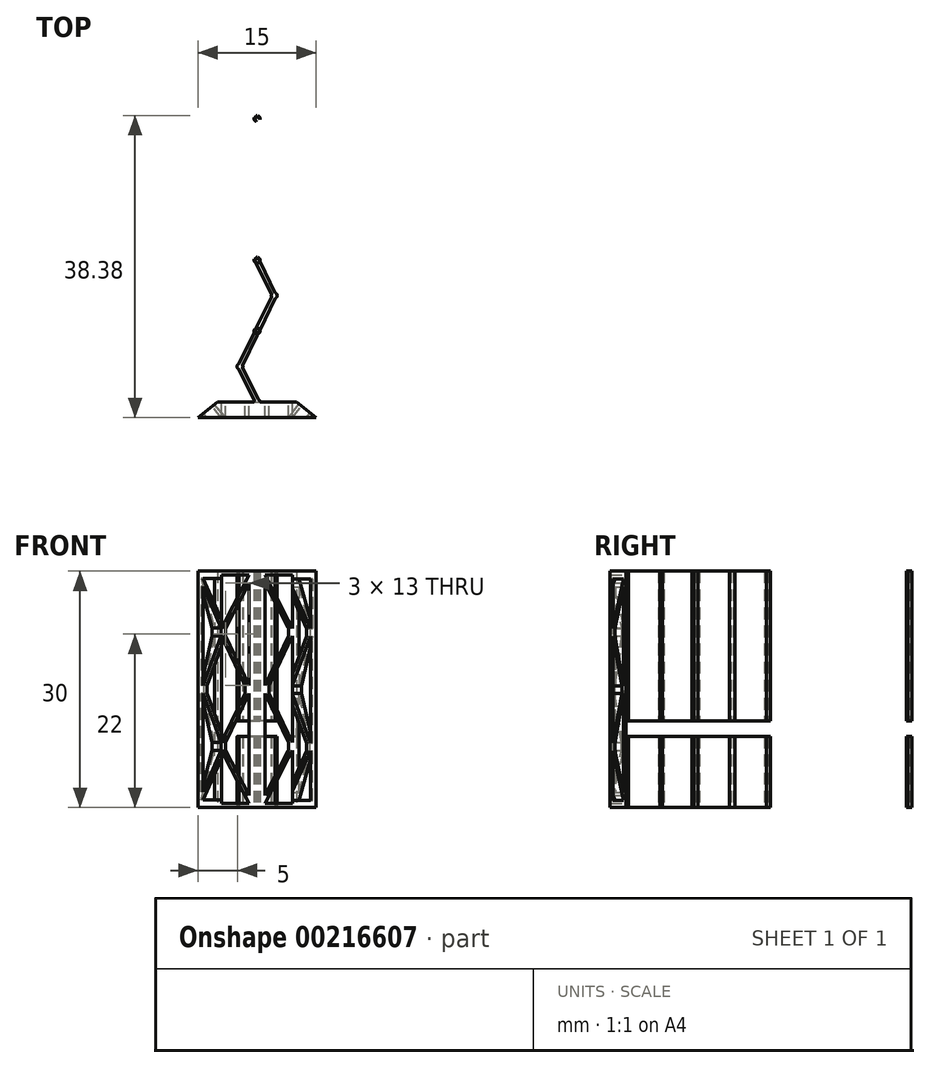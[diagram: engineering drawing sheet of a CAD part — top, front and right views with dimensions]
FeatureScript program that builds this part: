
annotation { "Feature Type Name" : "Feature", "Feature Type Description" : "" }
export const myFeature = defineFeature(function(context is Context, id is Id, definition is map)
    precondition{}
    {
        {
            var Q0;
            Q0=qCreatedBy(makeId("Top.planeOp"),FACE);
            var sketch = newSketch(context, id + "F0", { "sketchPlane" : qUnion([Q0])});
            skLineSegment(sketch, "E0", {"start": v(0, 0) * mm, "end": v(-7.5, 0) * mm});
            skLineSegment(sketch, "E1", {"start": v(0, 0) * mm, "end": v(7.5, 0) * mm});
            skLineSegment(sketch, "E2", {"start": v(0, 0) * mm, "end": v(0, 2) * mm});
            skLineSegment(sketch, "E3", {"start": v(0, 2) * mm, "end": v(-5, 2) * mm});
            skLineSegment(sketch, "E4", {"start": v(-5, 2) * mm, "end": v(-7.5, 0) * mm});
            skLineSegment(sketch, "E5", {"start": v(0, 2) * mm, "end": v(5, 2) * mm});
            skLineSegment(sketch, "E6", {"start": v(5, 2) * mm, "end": v(7.5, 0) * mm});
            skSolve(sketch);
        }
        {
            var Q0;
            Q0=makeQuery(id+"F0.imprint","IMPRINT",FACE,{"disambiguationData":[TD([[makeQuery(id+"F0.imprint","IMPRINT",EDGE,{"derivedFrom":sQuery(id+"F0.wireOp",EDGE,"E0")}),-1.0]])]});
            var Q1;
            Q1=makeQuery(id+"F0.imprint","IMPRINT",FACE,{"disambiguationData":[TD([[makeQuery(id+"F0.imprint","IMPRINT",EDGE,{"derivedFrom":sQuery(id+"F0.wireOp",EDGE,"E1")}),1.0]])]});
            extrude(context, id + "F1", {"entities" : qUnion([Q0, Q1]), "depth" : 30 * mm});
        }
        {
            var Q0;
            Q0=makeQuery(id+"F1.opExtrude","SWEPT_FACE",FACE,{"disambiguationData":[OSD([sQuery(id+"F0.wireOp",EDGE,"E3"),sQuery(id+"F0.wireOp",EDGE,"E5")])]});
            var sketch = newSketch(context, id + "F2", { "sketchPlane" : qUnion([Q0])});
            skLineSegment(sketch, "E7", {"start": v(-5, 30) * mm, "end": v(-5, 29.5) * mm});
            skLineSegment(sketch, "E8", {"start": v(-5, 30) * mm, "end": v(0, 30) * mm});
            skLineSegment(sketch, "E9", {"start": v(0, 30) * mm, "end": v(-1, 30) * mm});
            skLineSegment(sketch, "E10", {"start": v(-5, 29.5) * mm, "end": v(-4.5, 29.5) * mm});
            skLineSegment(sketch, "E11", {"start": v(-1, 30) * mm, "end": v(-5, 30) * mm});
            skLineSegment(sketch, "E12", {"start": v(-5, 29.5) * mm, "end": v(-5, 0) * mm});
            skLineSegment(sketch, "E13", {"start": v(-1, 30) * mm, "end": v(-1, 0) * mm});
            skLineSegment(sketch, "E14", {"start": v(0, 0) * mm, "end": v(-1, 0) * mm});
            skLineSegment(sketch, "E15", {"start": v(-1, 0) * mm, "end": v(-5, 0) * mm});
            skLineSegment(sketch, "E16", {"start": v(-5, 0) * mm, "end": v(-5, 0.5) * mm});
            skLineSegment(sketch, "E17", {"start": v(-5, 0.5) * mm, "end": v(-5, 29.5) * mm});
            skLineSegment(sketch, "E18", {"start": v(-5, 0.5) * mm, "end": v(-4.5, 0.5) * mm});
            skLineSegment(sketch, "E19", {"start": v(-4.5, 29.5) * mm, "end": v(-1, 29.5) * mm});
            skLineSegment(sketch, "E20", {"start": v(-4.5, 0.5) * mm, "end": v(-4.5, 0) * mm});
            skLineSegment(sketch, "E21", {"start": v(-4.5, 0.5) * mm, "end": v(-1, 0.5) * mm});
            skLineSegment(sketch, "E22", {"start": v(-4.5, 15) * mm, "end": v(-1, 15) * mm});
            skLineSegment(sketch, "E23", {"start": v(-4.5, 29.5) * mm, "end": v(-4.5, 15) * mm});
            skLineSegment(sketch, "E24", {"start": v(-4.5, 22.25) * mm, "end": v(-4.5, 22.75) * mm});
            skLineSegment(sketch, "E25", {"start": v(-4.5, 22.25) * mm, "end": v(-4.5, 21.75) * mm});
            skLineSegment(sketch, "E26", {"start": v(-1, 29.5) * mm, "end": v(-4.5, 22.75) * mm});
            skLineSegment(sketch, "E27", {"start": v(-1, 15) * mm, "end": v(-1, 15.5) * mm});
            skLineSegment(sketch, "E28", {"start": v(-1, 29.5) * mm, "end": v(-1, 28.5) * mm});
            skLineSegment(sketch, "E29", {"start": v(-4.5, 22.75) * mm, "end": v(-4, 22.75) * mm});
            skLineSegment(sketch, "E30", {"start": v(-4, 22.75) * mm, "end": v(-1, 28.5) * mm});
            skLineSegment(sketch, "E31", {"start": v(-4, 22.75) * mm, "end": v(-4, 21.75) * mm});
            skLineSegment(sketch, "E32", {"start": v(-4, 21.75) * mm, "end": v(-1, 15.5) * mm});
            skLineSegment(sketch, "E33", {"start": v(-1, 15.5) * mm, "end": v(-1.5, 15.5) * mm});
            skLineSegment(sketch, "E34", {"start": v(-1.5, 15.5) * mm, "end": v(-4.5, 21.75) * mm});
            skLineSegment(sketch, "E35", {"start": v(-1.5, 15.5) * mm, "end": v(-1.5, 15) * mm});
            skLineSegment(sketch, "E36.MirrorCS", {"start": v(-1, 15) * mm, "end": v(-1, 14.5) * mm});
            skLineSegment(sketch, "E37.MirrorCS", {"start": v(-1, 14.5) * mm, "end": v(-1.5, 14.5) * mm});
            skLineSegment(sketch, "E38.MirrorCS", {"start": v(-1.5, 14.5) * mm, "end": v(-1.5, 15) * mm});
            skLineSegment(sketch, "E39.MirrorCS", {"start": v(-4.5, 7.75) * mm, "end": v(-4.5, 8.25) * mm});
            skLineSegment(sketch, "E40.MirrorCS", {"start": v(-4, 7.25) * mm, "end": v(-4, 8.25) * mm});
            skLineSegment(sketch, "E41.MirrorCS", {"start": v(-1, 0.5) * mm, "end": v(-1, 1.5) * mm});
            skLineSegment(sketch, "E42.MirrorCS", {"start": v(-5, 0) * mm, "end": v(0, 0) * mm});
            skLineSegment(sketch, "E43.MirrorCS", {"start": v(-1.5, 14.5) * mm, "end": v(-4.5, 8.25) * mm});
            skLineSegment(sketch, "E44.MirrorCS", {"start": v(-4.5, 0.5) * mm, "end": v(-4.5, 15) * mm});
            skLineSegment(sketch, "E45.MirrorCS", {"start": v(-4, 8.25) * mm, "end": v(-1, 14.5) * mm});
            skLineSegment(sketch, "E46.MirrorCS", {"start": v(-1, 0.5) * mm, "end": v(-4.5, 7.25) * mm});
            skLineSegment(sketch, "E47.MirrorCS", {"start": v(-4, 7.25) * mm, "end": v(-1, 1.5) * mm});
            skLineSegment(sketch, "E48.MirrorCS", {"start": v(-4.5, 7.75) * mm, "end": v(-4.5, 7.25) * mm});
            skLineSegment(sketch, "E49.MirrorCS", {"start": v(-4.5, 7.25) * mm, "end": v(-4, 7.25) * mm});
            skLineSegment(sketch, "E50.MirrorCS", {"start": v(5, 0) * mm, "end": v(5, 0.5) * mm});
            skLineSegment(sketch, "E51.MirrorCS", {"start": v(5, 0.5) * mm, "end": v(4.5, 0.5) * mm});
            skLineSegment(sketch, "E52.MirrorCS", {"start": v(4.5, 0.5) * mm, "end": v(4.5, 0) * mm});
            skLineSegment(sketch, "E53.MirrorCS", {"start": v(4.5, 22.75) * mm, "end": v(4, 22.75) * mm});
            skLineSegment(sketch, "E54.MirrorCS", {"start": v(5, 29.5) * mm, "end": v(4.5, 29.5) * mm});
            skLineSegment(sketch, "E55.MirrorCS", {"start": v(5, 30) * mm, "end": v(5, 29.5) * mm});
            skLineSegment(sketch, "E56.MirrorCS", {"start": v(1, 15.5) * mm, "end": v(1.5, 15.5) * mm});
            skLineSegment(sketch, "E57.MirrorCS", {"start": v(4.5, 7.25) * mm, "end": v(4, 7.25) * mm});
            skLineSegment(sketch, "E58.MirrorCS", {"start": v(1.5, 14.5) * mm, "end": v(1.5, 15) * mm});
            skLineSegment(sketch, "E59.MirrorCS", {"start": v(1, 14.5) * mm, "end": v(1.5, 14.5) * mm});
            skLineSegment(sketch, "E60.MirrorCS", {"start": v(1.5, 15.5) * mm, "end": v(1.5, 15) * mm});
            skLineSegment(sketch, "E61.MirrorCS", {"start": v(4.5, 22.25) * mm, "end": v(4.5, 22.75) * mm});
            skLineSegment(sketch, "E62.MirrorCS", {"start": v(1, 15) * mm, "end": v(1, 14.5) * mm});
            skLineSegment(sketch, "E63.MirrorCS", {"start": v(1, 15) * mm, "end": v(1, 15.5) * mm});
            skLineSegment(sketch, "E64.MirrorCS", {"start": v(4.5, 7.75) * mm, "end": v(4.5, 7.25) * mm});
            skLineSegment(sketch, "E65.MirrorCS", {"start": v(4, 7.25) * mm, "end": v(4, 8.25) * mm});
            skLineSegment(sketch, "E66.MirrorCS", {"start": v(4.5, 7.75) * mm, "end": v(4.5, 8.25) * mm});
            skLineSegment(sketch, "E67.MirrorCS", {"start": v(4.5, 22.25) * mm, "end": v(4.5, 21.75) * mm});
            skLineSegment(sketch, "E68.MirrorCS", {"start": v(1, 0.5) * mm, "end": v(1, 1.5) * mm});
            skLineSegment(sketch, "E69.MirrorCS", {"start": v(1, 29.5) * mm, "end": v(1, 28.5) * mm});
            skLineSegment(sketch, "E70.MirrorCS", {"start": v(4, 22.75) * mm, "end": v(4, 21.75) * mm});
            skLineSegment(sketch, "E71.MirrorCS", {"start": v(1, 0) * mm, "end": v(5, 0) * mm});
            skLineSegment(sketch, "E72.MirrorCS", {"start": v(4.5, 0.5) * mm, "end": v(1, 0.5) * mm});
            skLineSegment(sketch, "E73.MirrorCS", {"start": v(5, 29.5) * mm, "end": v(5, 0) * mm});
            skLineSegment(sketch, "E74.MirrorCS", {"start": v(1, 29.5) * mm, "end": v(4.5, 22.75) * mm});
            skLineSegment(sketch, "E75.MirrorCS", {"start": v(1, 0.5) * mm, "end": v(4.5, 7.25) * mm});
            skLineSegment(sketch, "E76.MirrorCS", {"start": v(1.5, 14.5) * mm, "end": v(4.5, 8.25) * mm});
            skLineSegment(sketch, "E77.MirrorCS", {"start": v(4.5, 29.5) * mm, "end": v(1, 29.5) * mm});
            skLineSegment(sketch, "E78.MirrorCS", {"start": v(4, 21.75) * mm, "end": v(1, 15.5) * mm});
            skLineSegment(sketch, "E79.MirrorCS", {"start": v(5, 0.5) * mm, "end": v(5, 29.5) * mm});
            skLineSegment(sketch, "E80.MirrorCS", {"start": v(4, 8.25) * mm, "end": v(1, 14.5) * mm});
            skLineSegment(sketch, "E81.MirrorCS", {"start": v(4, 7.25) * mm, "end": v(1, 1.5) * mm});
            skLineSegment(sketch, "E82.MirrorCS", {"start": v(1.5, 15.5) * mm, "end": v(4.5, 21.75) * mm});
            skLineSegment(sketch, "E83.MirrorCS", {"start": v(4.5, 0.5) * mm, "end": v(4.5, 15) * mm});
            skLineSegment(sketch, "E84.MirrorCS", {"start": v(1, 30) * mm, "end": v(5, 30) * mm});
            skLineSegment(sketch, "E85.MirrorCS", {"start": v(4.5, 15) * mm, "end": v(1, 15) * mm});
            skLineSegment(sketch, "E86.MirrorCS", {"start": v(1, 30) * mm, "end": v(1, 0) * mm});
            skLineSegment(sketch, "E87.MirrorCS", {"start": v(4, 22.75) * mm, "end": v(1, 28.5) * mm});
            skLineSegment(sketch, "E88.MirrorCS", {"start": v(4.5, 29.5) * mm, "end": v(4.5, 15) * mm});
            skSolve(sketch);
        }
        {
            var Q0;
            {var subQ0=sQuery(id+"F2.wireOp",EDGE,"E19");Q0=makeQuery(id+"F2.imprint","IMPRINT",FACE,{"disambiguationData":[TD([[makeQuery(id+"F2.imprint","IMPRINT",EDGE,{"derivedFrom":subQ0}),-1.0]])]});}
            var Q1;
            {var subQ2=sQuery(id+"F2.wireOp",EDGE,"E30");Q1=makeQuery(id+"F2.imprint","IMPRINT",FACE,{"disambiguationData":[TD([[makeQuery(id+"F2.imprint","IMPRINT",EDGE,{"derivedFrom":subQ2}),-1.0]])]});}
            var Q2;
            {var subQ4=sQuery(id+"F2.wireOp",EDGE,"E34");Q2=makeQuery(id+"F2.imprint","IMPRINT",FACE,{"disambiguationData":[TD([[makeQuery(id+"F2.imprint","IMPRINT",EDGE,{"derivedFrom":subQ4}),1.0]])]});}
            var Q3;
            Q3=makeQuery(id+"F2.imprint","IMPRINT",FACE,{"disambiguationData":[TD([[makeQuery(id+"F2.imprint","IMPRINT",EDGE,{"derivedFrom":sQuery(id+"F2.wireOp",EDGE,"E70.MirrorCS")}),-1.0]])]});
            var Q4;
            {var subQ0=sQuery(id+"F2.wireOp",EDGE,"E74.MirrorCS");Q4=makeQuery(id+"F2.imprint","IMPRINT",FACE,{"disambiguationData":[TD([[makeQuery(id+"F2.imprint","IMPRINT",EDGE,{"derivedFrom":subQ0}),1.0]])]});}
            var Q5;
            {var subQ0=sQuery(id+"F2.wireOp",EDGE,"E60.MirrorCS");Q5=makeQuery(id+"F2.imprint","IMPRINT",FACE,{"disambiguationData":[TD([[makeQuery(id+"F2.imprint","IMPRINT",EDGE,{"derivedFrom":subQ0}),1.0]])]});}
            var Q6;
            {var subQ3=sQuery(id+"F2.wireOp",EDGE,"E38.MirrorCS");Q6=makeQuery(id+"F2.imprint","IMPRINT",FACE,{"disambiguationData":[TD([[makeQuery(id+"F2.imprint","IMPRINT",EDGE,{"derivedFrom":subQ3}),1.0]])]});}
            var Q7;
            Q7=makeQuery(id+"F2.imprint","IMPRINT",FACE,{"disambiguationData":[TD([[makeQuery(id+"F2.imprint","IMPRINT",EDGE,{"derivedFrom":sQuery(id+"F2.wireOp",EDGE,"E40.MirrorCS")}),-1.0]])]});
            var Q8;
            {var subQ0=sQuery(id+"F2.wireOp",EDGE,"E21");Q8=makeQuery(id+"F2.imprint","IMPRINT",FACE,{"disambiguationData":[TD([[makeQuery(id+"F2.imprint","IMPRINT",EDGE,{"derivedFrom":subQ0}),1.0]])]});}
            var Q9;
            Q9=makeQuery(id+"F2.imprint","IMPRINT",FACE,{"disambiguationData":[TD([[makeQuery(id+"F2.imprint","IMPRINT",EDGE,{"derivedFrom":sQuery(id+"F2.wireOp",EDGE,"E65.MirrorCS")}),1.0]])]});
            var Q10;
            {var subQ0=sQuery(id+"F2.wireOp",EDGE,"E58.MirrorCS");Q10=makeQuery(id+"F2.imprint","IMPRINT",FACE,{"disambiguationData":[TD([[makeQuery(id+"F2.imprint","IMPRINT",EDGE,{"derivedFrom":subQ0}),-1.0]])]});}
            var Q11;
            {var subQ0=sQuery(id+"F2.wireOp",EDGE,"E75.MirrorCS");Q11=makeQuery(id+"F2.imprint","IMPRINT",FACE,{"disambiguationData":[TD([[makeQuery(id+"F2.imprint","IMPRINT",EDGE,{"derivedFrom":subQ0}),-1.0]])]});}
            extrude(context, id + "F3", {"entities" : qUnion([Q0, Q1, Q2, Q3, Q4, Q5, Q6, Q7, Q8, Q9, Q10, Q11]), "operationType" : NewBodyOperationType.REMOVE, "oppositeDirection" : true, "depth" : 25 * mm});
        }
        {
            var Q0;
            Q0=makeQuery(id+"F1.opExtrude","SWEPT_FACE",FACE,{"disambiguationData":[OSD([sQuery(id+"F0.wireOp",EDGE,"E4")])]});
            var sketch = newSketch(context, id + "F4", { "sketchPlane" : qUnion([Q0])});
            skLineSegment(sketch, "E89", {"start": v(2.65, 30) * mm, "end": v(2.65, 0) * mm});
            skLineSegment(sketch, "E90.bottom", {"start": v(2.65, 30) * mm, "end": v(5.86, 30) * mm});
            skLineSegment(sketch, "E90.top", {"start": v(3.15, 15) * mm, "end": v(4.96, 15) * mm});
            skLineSegment(sketch, "E90.left", {"start": v(2.65, 30) * mm, "end": v(2.65, 15) * mm});
            skLineSegment(sketch, "E90.right", {"start": v(5.86, 30) * mm, "end": v(5.86, 15) * mm});
            skLineSegment(sketch, "E91", {"start": v(2.65, 30) * mm, "end": v(3.15, 30) * mm});
            skLineSegment(sketch, "E92", {"start": v(5.86, 15) * mm, "end": v(5.86, 15) * mm});
            skLineSegment(sketch, "E93.bottom", {"start": v(3.15, 29.07) * mm, "end": v(5.36, 29.07) * mm});
            skLineSegment(sketch, "E93.left", {"start": v(3.15, 29.07) * mm, "end": v(3.15, 22.78) * mm});
            skLineSegment(sketch, "E93.right", {"start": v(5.36, 28.07) * mm, "end": v(5.36, 15.5) * mm});
            skLineSegment(sketch, "E94", {"start": v(5.36, 15.5) * mm, "end": v(5.36, 16) * mm});
            skLineSegment(sketch, "E95", {"start": v(3.55, 22.78) * mm, "end": v(3.55, 21.78) * mm});
            skLineSegment(sketch, "E96", {"start": v(5.36, 29.07) * mm, "end": v(3.15, 22.78) * mm});
            skLineSegment(sketch, "E97", {"start": v(5.36, 28.07) * mm, "end": v(3.55, 22.78) * mm});
            skLineSegment(sketch, "E98", {"start": v(3.15, 15.5) * mm, "end": v(3.15, 15) * mm});
            skLineSegment(sketch, "E99", {"start": v(4.96, 15.5) * mm, "end": v(4.96, 15) * mm});
            skLineSegment(sketch, "E100", {"start": v(3.15, 21.78) * mm, "end": v(4.96, 15.5) * mm});
            skLineSegment(sketch, "E101", {"start": v(3.55, 21.78) * mm, "end": v(5.36, 15.5) * mm});
            skLineSegment(sketch, "E102.trimOffspring", {"start": v(3.15, 21.78) * mm, "end": v(3.15, 15.5) * mm});
            skLineSegment(sketch, "E103.MirrorCS", {"start": v(3.15, 14.5) * mm, "end": v(3.15, 15) * mm});
            skLineSegment(sketch, "E104.MirrorCS", {"start": v(4.96, 14.5) * mm, "end": v(4.96, 15) * mm});
            skLineSegment(sketch, "E105.MirrorCS", {"start": v(5.36, 14.5) * mm, "end": v(5.36, 14) * mm});
            skLineSegment(sketch, "E106.MirrorCS", {"start": v(3.15, 15) * mm, "end": v(5.86, 15) * mm});
            skLineSegment(sketch, "E107.MirrorCS", {"start": v(2.65, 0) * mm, "end": v(3.15, 0) * mm});
            skLineSegment(sketch, "E108.MirrorCS", {"start": v(3.55, 8.22) * mm, "end": v(5.36, 14.5) * mm});
            skLineSegment(sketch, "E109.MirrorCS", {"start": v(5.36, 0.93) * mm, "end": v(3.15, 7.22) * mm});
            skLineSegment(sketch, "E110.MirrorCS", {"start": v(2.65, 0) * mm, "end": v(5.86, 0) * mm});
            skLineSegment(sketch, "E111.MirrorCS", {"start": v(5.36, 1.93) * mm, "end": v(3.55, 7.22) * mm});
            skLineSegment(sketch, "E112.MirrorCS", {"start": v(2.65, 0) * mm, "end": v(2.65, 15) * mm});
            skLineSegment(sketch, "E113.MirrorCS", {"start": v(3.15, 8.22) * mm, "end": v(3.15, 14.5) * mm});
            skLineSegment(sketch, "E114.MirrorCS", {"start": v(3.15, 0.93) * mm, "end": v(5.36, 0.93) * mm});
            skLineSegment(sketch, "E115.MirrorCS", {"start": v(5.86, 0) * mm, "end": v(5.86, 15) * mm});
            skLineSegment(sketch, "E116.MirrorCS", {"start": v(5.36, 1.93) * mm, "end": v(5.36, 14.5) * mm});
            skLineSegment(sketch, "E117.MirrorCS", {"start": v(3.15, 0.93) * mm, "end": v(3.15, 7.22) * mm});
            skLineSegment(sketch, "E118.MirrorCS", {"start": v(3.15, 8.22) * mm, "end": v(4.96, 14.5) * mm});
            skLineSegment(sketch, "E119.MirrorCS", {"start": v(3.55, 7.22) * mm, "end": v(3.55, 8.22) * mm});
            skPoint(sketch, "E120.orphan", {"position": v(2.65, 15) * mm});
            skSolve(sketch);
        }
        {
            var Q0;
            {var subQ2=sQuery(id+"F4.wireOp",EDGE,"E98");Q0=makeQuery(id+"F4.imprint","IMPRINT",FACE,{"disambiguationData":[TD([[makeQuery(id+"F4.imprint","IMPRINT",EDGE,{"derivedFrom":subQ2}),1.0]])]});}
            var Q1;
            Q1=makeQuery(id+"F4.imprint","IMPRINT",FACE,{"disambiguationData":[TD([[makeQuery(id+"F4.imprint","IMPRINT",EDGE,{"derivedFrom":sQuery(id+"F4.wireOp",EDGE,"E93.right")}),-1.0]])]});
            var Q2;
            {var subQ2=sQuery(id+"F4.wireOp",EDGE,"E103.MirrorCS");Q2=makeQuery(id+"F4.imprint","IMPRINT",FACE,{"disambiguationData":[TD([[makeQuery(id+"F4.imprint","IMPRINT",EDGE,{"derivedFrom":subQ2}),-1.0]])]});}
            var Q3;
            {var subQ1=sQuery(id+"F4.wireOp",EDGE,"E108.MirrorCS");Q3=makeQuery(id+"F4.imprint","IMPRINT",FACE,{"disambiguationData":[TD([[makeQuery(id+"F4.imprint","IMPRINT",EDGE,{"derivedFrom":subQ1}),-1.0]])]});}
            var Q4;
            Q4=makeQuery(id+"F4.imprint","IMPRINT",FACE,{"disambiguationData":[TD([[makeQuery(id+"F4.imprint","IMPRINT",EDGE,{"derivedFrom":sQuery(id+"F4.wireOp",EDGE,"E109.MirrorCS")}),1.0]])]});
            var Q5;
            Q5=makeQuery(id+"F4.imprint","IMPRINT",FACE,{"disambiguationData":[TD([[makeQuery(id+"F4.imprint","IMPRINT",EDGE,{"derivedFrom":sQuery(id+"F4.wireOp",EDGE,"E93.bottom")}),-1.0]])]});
            extrude(context, id + "F5", {"entities" : qUnion([Q0, Q1, Q2, Q3, Q4, Q5]), "operationType" : NewBodyOperationType.REMOVE, "oppositeDirection" : true, "depth" : 25 * mm});
        }
        {
            var Q0;
            Q0=makeQuery(id+"F1.opExtrude","SWEPT_FACE",FACE,{"disambiguationData":[OSD([sQuery(id+"F0.wireOp",EDGE,"E6")])]});
            var sketch = newSketch(context, id + "F6", { "sketchPlane" : qUnion([Q0])});
            skLineSegment(sketch, "E121", {"start": v(-5.79, 29.95) * mm, "end": v(-5.79, -0.05) * mm});
            skLineSegment(sketch, "E122.bottom", {"start": v(-5.79, 29.95) * mm, "end": v(-2.58, 29.95) * mm});
            skLineSegment(sketch, "E122.top", {"start": v(-5.29, 14.95) * mm, "end": v(-3.48, 14.95) * mm});
            skLineSegment(sketch, "E122.left", {"start": v(-5.79, 29.95) * mm, "end": v(-5.79, 14.95) * mm});
            skLineSegment(sketch, "E122.right", {"start": v(-2.58, 29.95) * mm, "end": v(-2.58, 14.95) * mm});
            skLineSegment(sketch, "E123", {"start": v(-5.79, 29.95) * mm, "end": v(-5.29, 29.95) * mm});
            skLineSegment(sketch, "E124", {"start": v(4.95, 14.95) * mm, "end": v(-2.58, 14.95) * mm});
            skLineSegment(sketch, "E125.bottom", {"start": v(-5.29, 29.02) * mm, "end": v(-3.08, 29.02) * mm});
            skLineSegment(sketch, "E125.left", {"start": v(-5.29, 29.02) * mm, "end": v(-5.29, 22.74) * mm});
            skLineSegment(sketch, "E125.right", {"start": v(-3.08, 28.02) * mm, "end": v(-3.08, 15.45) * mm});
            skLineSegment(sketch, "E126", {"start": v(-3.08, 14.82) * mm, "end": v(-3.08, 15.45) * mm});
            skLineSegment(sketch, "E127", {"start": v(-4.89, 22.74) * mm, "end": v(-4.89, 21.74) * mm});
            skLineSegment(sketch, "E128", {"start": v(-3.08, 29.02) * mm, "end": v(-5.29, 22.74) * mm});
            skLineSegment(sketch, "E129", {"start": v(-3.08, 28.02) * mm, "end": v(-4.89, 22.74) * mm});
            skLineSegment(sketch, "E130", {"start": v(-5.29, 16.58) * mm, "end": v(-5.29, 14.95) * mm});
            skLineSegment(sketch, "E131", {"start": v(-3.48, 15.45) * mm, "end": v(-3.48, 14.95) * mm});
            skLineSegment(sketch, "E132", {"start": v(-5.29, 21.74) * mm, "end": v(-3.48, 15.45) * mm});
            skLineSegment(sketch, "E133", {"start": v(-4.89, 21.74) * mm, "end": v(-3.08, 15.45) * mm});
            skLineSegment(sketch, "E134.trimOffspring", {"start": v(-5.29, 21.74) * mm, "end": v(-5.29, 16.58) * mm});
            skLineSegment(sketch, "E135.MirrorCS", {"start": v(-5.29, 13.32) * mm, "end": v(-5.29, 14.95) * mm});
            skLineSegment(sketch, "E136.MirrorCS", {"start": v(-3.48, 14.45) * mm, "end": v(-3.48, 14.95) * mm});
            skLineSegment(sketch, "E137.MirrorCS", {"start": v(-3.08, 15.08) * mm, "end": v(-3.08, 14.45) * mm});
            skLineSegment(sketch, "E138.MirrorCS", {"start": v(-5.29, 14.95) * mm, "end": v(-2.58, 14.95) * mm});
            skLineSegment(sketch, "E139.MirrorCS", {"start": v(-5.79, -0.05) * mm, "end": v(-5.29, -0.05) * mm});
            skLineSegment(sketch, "E140.MirrorCS", {"start": v(-4.89, 8.17) * mm, "end": v(-3.08, 14.45) * mm});
            skLineSegment(sketch, "E141.MirrorCS", {"start": v(-3.08, 0.89) * mm, "end": v(-5.29, 7.17) * mm});
            skLineSegment(sketch, "E142.MirrorCS", {"start": v(-5.79, -0.05) * mm, "end": v(-2.58, -0.05) * mm});
            skLineSegment(sketch, "E143.MirrorCS", {"start": v(-3.08, 1.89) * mm, "end": v(-4.89, 7.17) * mm});
            skLineSegment(sketch, "E144.MirrorCS", {"start": v(-5.79, -0.05) * mm, "end": v(-5.79, 14.95) * mm});
            skLineSegment(sketch, "E145.MirrorCS", {"start": v(-5.29, 8.17) * mm, "end": v(-5.29, 13.32) * mm});
            skLineSegment(sketch, "E146.MirrorCS", {"start": v(-5.29, 0.89) * mm, "end": v(-3.08, 0.89) * mm});
            skLineSegment(sketch, "E147.MirrorCS", {"start": v(-2.58, -0.05) * mm, "end": v(-2.58, 14.95) * mm});
            skLineSegment(sketch, "E148.MirrorCS", {"start": v(-3.08, 1.89) * mm, "end": v(-3.08, 14.45) * mm});
            skLineSegment(sketch, "E149.MirrorCS", {"start": v(-5.29, 0.89) * mm, "end": v(-5.29, 7.17) * mm});
            skLineSegment(sketch, "E150.MirrorCS", {"start": v(-5.29, 8.17) * mm, "end": v(-3.48, 14.45) * mm});
            skLineSegment(sketch, "E151.MirrorCS", {"start": v(-4.89, 7.17) * mm, "end": v(-4.89, 8.17) * mm});
            skPoint(sketch, "E152.orphan", {"position": v(-5.79, 14.95) * mm});
            skSolve(sketch);
        }
        {
            var Q0;
            Q0=makeQuery(id+"F6.imprint","IMPRINT",FACE,{"disambiguationData":[TD([[makeQuery(id+"F6.imprint","IMPRINT",EDGE,{"derivedFrom":sQuery(id+"F6.wireOp",EDGE,"E140.MirrorCS")}),-1.0]])]});
            var Q1;
            {var subQ1=sQuery(id+"F6.wireOp",EDGE,"E135.MirrorCS");Q1=makeQuery(id+"F6.imprint","IMPRINT",FACE,{"disambiguationData":[TD([[makeQuery(id+"F6.imprint","IMPRINT",EDGE,{"derivedFrom":subQ1}),-1.0]])]});}
            var Q2;
            {var subQ1=sQuery(id+"F6.wireOp",EDGE,"E130");Q2=makeQuery(id+"F6.imprint","IMPRINT",FACE,{"disambiguationData":[TD([[makeQuery(id+"F6.imprint","IMPRINT",EDGE,{"derivedFrom":subQ1}),1.0]])]});}
            var Q3;
            Q3=makeQuery(id+"F6.imprint","IMPRINT",FACE,{"disambiguationData":[TD([[makeQuery(id+"F6.imprint","IMPRINT",EDGE,{"derivedFrom":sQuery(id+"F6.wireOp",EDGE,"E141.MirrorCS")}),1.0]])]});
            var Q4;
            Q4=makeQuery(id+"F6.imprint","IMPRINT",FACE,{"disambiguationData":[TD([[makeQuery(id+"F6.imprint","IMPRINT",EDGE,{"derivedFrom":sQuery(id+"F6.wireOp",EDGE,"E125.right")}),-1.0]])]});
            var Q5;
            Q5=makeQuery(id+"F6.imprint","IMPRINT",FACE,{"disambiguationData":[TD([[makeQuery(id+"F6.imprint","IMPRINT",EDGE,{"derivedFrom":sQuery(id+"F6.wireOp",EDGE,"E125.bottom")}),-1.0]])]});
            extrude(context, id + "F7", {"entities" : qUnion([Q0, Q1, Q2, Q3, Q4, Q5]), "operationType" : NewBodyOperationType.REMOVE, "oppositeDirection" : true, "depth" : 25 * mm});
        }
        {
            var Q0;
            Q0=qCreatedBy(makeId("Top.planeOp"),FACE);
            var sketch = newSketch(context, id + "F8", { "sketchPlane" : qUnion([Q0])});
            skLineSegment(sketch, "E153", {"start": v(0, 0) * mm, "end": v(0, 2) * mm});
            skLineSegment(sketch, "E154", {"start": v(0, 2) * mm, "end": v(-2.18, 6.5) * mm});
            skLineSegment(sketch, "E155", {"start": v(-2.18, 6.5) * mm, "end": v(0, 11) * mm});
            skLineSegment(sketch, "E156", {"start": v(0, 11) * mm, "end": v(0, 2) * mm});
            skLineSegment(sketch, "E157.direction1", {"start": v(0, 2) * mm, "end": v(0, 2) * mm});
            skLineSegment(sketch, "E158", {"start": v(0, 2) * mm, "end": v(0.22, 2.1) * mm});
            skLineSegment(sketch, "E159", {"start": v(0, 2) * mm, "end": v(-0.23, 1.9) * mm});
            skLineSegment(sketch, "E160", {"start": v(-2.18, 6.5) * mm, "end": v(-2.4, 6.4) * mm});
            skLineSegment(sketch, "E161", {"start": v(-2.4, 6.4) * mm, "end": v(-0.23, 1.9) * mm});
            skLineSegment(sketch, "E162", {"start": v(-2.18, 6.5) * mm, "end": v(-1.95, 6.6) * mm});
            skLineSegment(sketch, "E163", {"start": v(-1.95, 6.6) * mm, "end": v(0.22, 2.1) * mm});
            skLineSegment(sketch, "E164", {"start": v(-2.18, 6.5) * mm, "end": v(-1.95, 6.4) * mm});
            skLineSegment(sketch, "E165", {"start": v(-2.18, 6.5) * mm, "end": v(-2.4, 6.6) * mm});
            skCircle(sketch, "E166", {"center": v(-2.18, 6.5) * mm, "radius": 0.38 * mm});
            skLineSegment(sketch, "E167", {"start": v(0, 11) * mm, "end": v(-0.23, 11.1) * mm});
            skLineSegment(sketch, "E168", {"start": v(-0.23, 11.1) * mm, "end": v(-2.4, 6.6) * mm});
            skLineSegment(sketch, "E169", {"start": v(0, 11) * mm, "end": v(0.22, 10.9) * mm});
            skLineSegment(sketch, "E170", {"start": v(0.22, 10.9) * mm, "end": v(-1.95, 6.4) * mm});
            skCircle(sketch, "E171", {"center": v(0, 11) * mm, "radius": 0.38 * mm});
            skLineSegment(sketch, "E172", {"start": v(-0.23, 11.1) * mm, "end": v(0.22, 10.9) * mm});
            skLineSegment(sketch, "E173", {"start": v(0.22, 10.9) * mm, "end": v(2.4, 15.4) * mm});
            skLineSegment(sketch, "E174", {"start": v(-0.23, 11.1) * mm, "end": v(1.95, 15.6) * mm});
            skLineSegment(sketch, "E175", {"start": v(1.95, 15.6) * mm, "end": v(2.4, 15.4) * mm});
            skCircle(sketch, "E176", {"center": v(2.18, 15.5) * mm, "radius": 0.38 * mm});
            skLineSegment(sketch, "E177", {"start": v(2.18, 15.5) * mm, "end": v(0, 20) * mm});
            skLineSegment(sketch, "E178", {"start": v(0, 20) * mm, "end": v(-0.23, 19.9) * mm});
            skLineSegment(sketch, "E179", {"start": v(2.18, 15.5) * mm, "end": v(1.95, 15.4) * mm});
            skLineSegment(sketch, "E180", {"start": v(2.18, 15.5) * mm, "end": v(2.4, 15.6) * mm});
            skLineSegment(sketch, "E181", {"start": v(1.95, 15.4) * mm, "end": v(-0.23, 19.9) * mm});
            skLineSegment(sketch, "E182", {"start": v(0, 20) * mm, "end": v(0.22, 20.1) * mm});
            skLineSegment(sketch, "E183", {"start": v(0.22, 20.1) * mm, "end": v(2.4, 15.6) * mm});
            skCircle(sketch, "E184", {"center": v(0, 20) * mm, "radius": 0.38 * mm});
            skCircle(sketch, "E185", {"center": v(0, 2) * mm, "radius": 0.38 * mm});
            skLineSegment(sketch, "E186.0.1.0", {"start": v(2.18, 33.5) * mm, "end": v(0, 38) * mm});
            skLineSegment(sketch, "E186.0.1.1", {"start": v(-1.95, 24.6) * mm, "end": v(0.23, 20.1) * mm});
            skLineSegment(sketch, "E186.0.1.2", {"start": v(1.95, 33.4) * mm, "end": v(-0.23, 37.9) * mm});
            skLineSegment(sketch, "E186.0.1.3", {"start": v(-2.4, 24.4) * mm, "end": v(-0.23, 19.9) * mm});
            skLineSegment(sketch, "E186.0.1.4", {"start": v(0, 29) * mm, "end": v(0, 20) * mm});
            skLineSegment(sketch, "E186.0.1.5", {"start": v(-2.18, 24.5) * mm, "end": v(0, 29) * mm});
            skLineSegment(sketch, "E186.0.1.6", {"start": v(-0.23, 29.1) * mm, "end": v(-2.4, 24.6) * mm});
            skLineSegment(sketch, "E186.0.1.7", {"start": v(0.22, 28.9) * mm, "end": v(-1.95, 24.4) * mm});
            skLineSegment(sketch, "E186.0.1.8", {"start": v(0.22, 38.1) * mm, "end": v(2.4, 33.6) * mm});
            skLineSegment(sketch, "E186.0.1.9", {"start": v(0.22, 28.9) * mm, "end": v(2.4, 33.4) * mm});
            skLineSegment(sketch, "E186.0.1.10", {"start": v(-0.23, 29.1) * mm, "end": v(1.95, 33.6) * mm});
            skLineSegment(sketch, "E186.0.1.11", {"start": v(0, 20) * mm, "end": v(-2.18, 24.5) * mm});
            skLineSegment(sketch, "E186.0.1.12", {"start": v(0, 20) * mm, "end": v(-2.18, 24.5) * mm});
            skLineSegment(sketch, "E186.0.1.13", {"start": v(0, 29) * mm, "end": v(0, 20) * mm});
            skLineSegment(sketch, "E186.0.1.14", {"start": v(-2.18, 24.5) * mm, "end": v(0, 29) * mm});
            skLineSegment(sketch, "E186.0.1.15", {"start": v(-2.18, 24.5) * mm, "end": v(0, 29) * mm});
            skLineSegment(sketch, "E186.0.1.16", {"start": v(0, 29) * mm, "end": v(0, 20) * mm});
            skLineSegment(sketch, "E186.0.1.17", {"start": v(0, 20) * mm, "end": v(-2.18, 24.5) * mm});
            skCircle(sketch, "E186.0.1.18", {"center": v(0, 38) * mm, "radius": 0.38 * mm});
            skCircle(sketch, "E186.0.1.19", {"center": v(2.18, 33.5) * mm, "radius": 0.38 * mm});
            skCircle(sketch, "E186.0.1.20", {"center": v(-2.18, 24.5) * mm, "radius": 0.38 * mm});
            skLineSegment(sketch, "E186.0.1.21", {"start": v(0, 38) * mm, "end": v(-0.23, 37.9) * mm});
            skLineSegment(sketch, "E186.0.1.22", {"start": v(0, 38) * mm, "end": v(0.22, 38.1) * mm});
            skLineSegment(sketch, "E186.0.1.23", {"start": v(2.18, 33.5) * mm, "end": v(2.4, 33.6) * mm});
            skLineSegment(sketch, "E186.0.1.24", {"start": v(1.95, 33.6) * mm, "end": v(2.4, 33.4) * mm});
            skLineSegment(sketch, "E186.0.1.25", {"start": v(2.18, 33.5) * mm, "end": v(1.95, 33.4) * mm});
            skLineSegment(sketch, "E186.0.1.26", {"start": v(0, 29) * mm, "end": v(0.22, 28.9) * mm});
            skLineSegment(sketch, "E186.0.1.27", {"start": v(-0.23, 29.1) * mm, "end": v(0.22, 28.9) * mm});
            skCircle(sketch, "E186.0.1.28", {"center": v(0, 29) * mm, "radius": 0.38 * mm});
            skLineSegment(sketch, "E186.0.1.29", {"start": v(0, 29) * mm, "end": v(-0.23, 29.1) * mm});
            skLineSegment(sketch, "E186.0.1.31", {"start": v(-2.18, 24.5) * mm, "end": v(-1.95, 24.6) * mm});
            skLineSegment(sketch, "E186.0.1.33", {"start": v(0, 20) * mm, "end": v(-0.22, 19.9) * mm});
            skLineSegment(sketch, "E186.0.1.34", {"start": v(-2.18, 24.5) * mm, "end": v(-1.95, 24.4) * mm});
            skLineSegment(sketch, "E186.0.1.35", {"start": v(-2.18, 24.5) * mm, "end": v(-2.4, 24.4) * mm});
            skLineSegment(sketch, "E186.0.1.36", {"start": v(-2.18, 24.5) * mm, "end": v(-2.4, 24.6) * mm});
            skLineSegment(sketch, "E186.1.0.16", {"start": v(0, 11) * mm, "end": v(0, 10.63) * mm});
            skLineSegment(sketch, "E186.1.1.0", {"start": v(2.18, 33.5) * mm, "end": v(0, 38) * mm});
            skLineSegment(sketch, "E186.1.1.1", {"start": v(-1.95, 24.6) * mm, "end": v(0.23, 20.1) * mm});
            skLineSegment(sketch, "E186.1.1.2", {"start": v(1.95, 33.4) * mm, "end": v(-0.23, 37.9) * mm});
            skLineSegment(sketch, "E186.1.1.3", {"start": v(-2.4, 24.4) * mm, "end": v(-0.23, 19.9) * mm});
            skLineSegment(sketch, "E186.1.1.4", {"start": v(0, 29) * mm, "end": v(0, 20) * mm});
            skLineSegment(sketch, "E186.1.1.5", {"start": v(-2.18, 24.5) * mm, "end": v(0, 29) * mm});
            skLineSegment(sketch, "E186.1.1.6", {"start": v(-0.23, 29.1) * mm, "end": v(-2.4, 24.6) * mm});
            skLineSegment(sketch, "E186.1.1.7", {"start": v(0.22, 28.9) * mm, "end": v(-1.95, 24.4) * mm});
            skLineSegment(sketch, "E186.1.1.8", {"start": v(0.22, 38.1) * mm, "end": v(2.4, 33.6) * mm});
            skLineSegment(sketch, "E186.1.1.9", {"start": v(0.22, 28.9) * mm, "end": v(2.4, 33.4) * mm});
            skLineSegment(sketch, "E186.1.1.10", {"start": v(-0.23, 29.1) * mm, "end": v(1.95, 33.6) * mm});
            skLineSegment(sketch, "E186.1.1.11", {"start": v(0, 20) * mm, "end": v(-2.18, 24.5) * mm});
            skLineSegment(sketch, "E186.1.1.12", {"start": v(0, 20) * mm, "end": v(-2.18, 24.5) * mm});
            skLineSegment(sketch, "E186.1.1.13", {"start": v(0, 29) * mm, "end": v(0, 20) * mm});
            skLineSegment(sketch, "E186.1.1.14", {"start": v(-2.18, 24.5) * mm, "end": v(0, 29) * mm});
            skLineSegment(sketch, "E186.1.1.15", {"start": v(-2.18, 24.5) * mm, "end": v(0, 29) * mm});
            skLineSegment(sketch, "E186.1.1.16", {"start": v(0, 29) * mm, "end": v(0, 20) * mm});
            skLineSegment(sketch, "E186.1.1.17", {"start": v(0, 20) * mm, "end": v(-2.18, 24.5) * mm});
            skCircle(sketch, "E186.1.1.18", {"center": v(0, 38) * mm, "radius": 0.38 * mm});
            skCircle(sketch, "E186.1.1.19", {"center": v(2.18, 33.5) * mm, "radius": 0.38 * mm});
            skCircle(sketch, "E186.1.1.20", {"center": v(-2.18, 24.5) * mm, "radius": 0.38 * mm});
            skLineSegment(sketch, "E186.1.1.21", {"start": v(0, 38) * mm, "end": v(-0.23, 37.9) * mm});
            skLineSegment(sketch, "E186.1.1.22", {"start": v(0, 38) * mm, "end": v(0.22, 38.1) * mm});
            skLineSegment(sketch, "E186.1.1.23", {"start": v(2.18, 33.5) * mm, "end": v(2.4, 33.6) * mm});
            skLineSegment(sketch, "E186.1.1.24", {"start": v(1.95, 33.6) * mm, "end": v(2.4, 33.4) * mm});
            skLineSegment(sketch, "E186.1.1.25", {"start": v(2.18, 33.5) * mm, "end": v(1.95, 33.4) * mm});
            skLineSegment(sketch, "E186.1.1.26", {"start": v(0, 29) * mm, "end": v(0.22, 28.9) * mm});
            skLineSegment(sketch, "E186.1.1.27", {"start": v(-0.23, 29.1) * mm, "end": v(0.22, 28.9) * mm});
            skCircle(sketch, "E186.1.1.28", {"center": v(0, 29) * mm, "radius": 0.38 * mm});
            skLineSegment(sketch, "E186.1.1.29", {"start": v(0, 29) * mm, "end": v(-0.23, 29.1) * mm});
            skLineSegment(sketch, "E186.1.1.31", {"start": v(-2.18, 24.5) * mm, "end": v(-1.95, 24.6) * mm});
            skLineSegment(sketch, "E186.1.1.33", {"start": v(0, 20) * mm, "end": v(-0.22, 19.9) * mm});
            skLineSegment(sketch, "E186.1.1.34", {"start": v(-2.18, 24.5) * mm, "end": v(-1.95, 24.4) * mm});
            skLineSegment(sketch, "E186.1.1.35", {"start": v(-2.18, 24.5) * mm, "end": v(-2.4, 24.4) * mm});
            skLineSegment(sketch, "E186.1.1.36", {"start": v(-2.18, 24.5) * mm, "end": v(-2.4, 24.6) * mm});
            skLineSegment(sketch, "E186.2.0.13", {"start": v(0, 11) * mm, "end": v(0, 10.43) * mm});
            skLineSegment(sketch, "E186.2.1.0", {"start": v(2.18, 33.5) * mm, "end": v(0, 38) * mm});
            skLineSegment(sketch, "E186.2.1.1", {"start": v(-1.95, 24.6) * mm, "end": v(0.23, 20.1) * mm});
            skLineSegment(sketch, "E186.2.1.2", {"start": v(1.95, 33.4) * mm, "end": v(-0.23, 37.9) * mm});
            skLineSegment(sketch, "E186.2.1.3", {"start": v(-2.4, 24.4) * mm, "end": v(-0.23, 19.9) * mm});
            skLineSegment(sketch, "E186.2.1.4", {"start": v(0, 29) * mm, "end": v(0, 20) * mm});
            skLineSegment(sketch, "E186.2.1.5", {"start": v(-2.18, 24.5) * mm, "end": v(0, 29) * mm});
            skLineSegment(sketch, "E186.2.1.6", {"start": v(-0.23, 29.1) * mm, "end": v(-2.4, 24.6) * mm});
            skLineSegment(sketch, "E186.2.1.7", {"start": v(0.22, 28.9) * mm, "end": v(-1.95, 24.4) * mm});
            skLineSegment(sketch, "E186.2.1.8", {"start": v(0.22, 38.1) * mm, "end": v(2.4, 33.6) * mm});
            skLineSegment(sketch, "E186.2.1.9", {"start": v(0.22, 28.9) * mm, "end": v(2.4, 33.4) * mm});
            skLineSegment(sketch, "E186.2.1.10", {"start": v(-0.23, 29.1) * mm, "end": v(1.95, 33.6) * mm});
            skLineSegment(sketch, "E186.2.1.11", {"start": v(0, 20) * mm, "end": v(-2.18, 24.5) * mm});
            skLineSegment(sketch, "E186.2.1.12", {"start": v(0, 20) * mm, "end": v(-2.18, 24.5) * mm});
            skLineSegment(sketch, "E186.2.1.13", {"start": v(0, 29) * mm, "end": v(0, 20) * mm});
            skLineSegment(sketch, "E186.2.1.14", {"start": v(-2.18, 24.5) * mm, "end": v(0, 29) * mm});
            skLineSegment(sketch, "E186.2.1.15", {"start": v(-2.18, 24.5) * mm, "end": v(0, 29) * mm});
            skLineSegment(sketch, "E186.2.1.16", {"start": v(0, 29) * mm, "end": v(0, 20) * mm});
            skLineSegment(sketch, "E186.2.1.17", {"start": v(0, 20) * mm, "end": v(-2.18, 24.5) * mm});
            skCircle(sketch, "E186.2.1.18", {"center": v(0, 38) * mm, "radius": 0.38 * mm});
            skCircle(sketch, "E186.2.1.19", {"center": v(2.18, 33.5) * mm, "radius": 0.38 * mm});
            skCircle(sketch, "E186.2.1.20", {"center": v(-2.18, 24.5) * mm, "radius": 0.38 * mm});
            skLineSegment(sketch, "E186.2.1.21", {"start": v(0, 38) * mm, "end": v(-0.23, 37.9) * mm});
            skLineSegment(sketch, "E186.2.1.22", {"start": v(0, 38) * mm, "end": v(0.22, 38.1) * mm});
            skLineSegment(sketch, "E186.2.1.23", {"start": v(2.18, 33.5) * mm, "end": v(2.4, 33.6) * mm});
            skLineSegment(sketch, "E186.2.1.24", {"start": v(1.95, 33.6) * mm, "end": v(2.4, 33.4) * mm});
            skLineSegment(sketch, "E186.2.1.25", {"start": v(2.18, 33.5) * mm, "end": v(1.95, 33.4) * mm});
            skLineSegment(sketch, "E186.2.1.26", {"start": v(0, 29) * mm, "end": v(0.22, 28.9) * mm});
            skLineSegment(sketch, "E186.2.1.27", {"start": v(-0.23, 29.1) * mm, "end": v(0.22, 28.9) * mm});
            skCircle(sketch, "E186.2.1.28", {"center": v(0, 29) * mm, "radius": 0.38 * mm});
            skLineSegment(sketch, "E186.2.1.29", {"start": v(0, 29) * mm, "end": v(-0.23, 29.1) * mm});
            skLineSegment(sketch, "E186.2.1.31", {"start": v(-2.18, 24.5) * mm, "end": v(-1.95, 24.6) * mm});
            skLineSegment(sketch, "E186.2.1.33", {"start": v(0, 20) * mm, "end": v(-0.22, 19.9) * mm});
            skLineSegment(sketch, "E186.2.1.34", {"start": v(-2.18, 24.5) * mm, "end": v(-1.95, 24.4) * mm});
            skLineSegment(sketch, "E186.2.1.35", {"start": v(-2.18, 24.5) * mm, "end": v(-2.4, 24.4) * mm});
            skLineSegment(sketch, "E186.2.1.36", {"start": v(-2.18, 24.5) * mm, "end": v(-2.4, 24.6) * mm});
            skLineSegment(sketch, "E186.direction1", {"start": v(-0.23, 1.9) * mm, "end": v(-0.23, 1.9) * mm});
            skLineSegment(sketch, "E186.direction2", {"start": v(-0.23, 1.9) * mm, "end": v(-0.23, 19.9) * mm, "construction": true});
            skLineSegment(sketch, "E187.trimOffspring", {"start": v(0, 2.57) * mm, "end": v(0, 2) * mm});
            skLineSegment(sketch, "E188.0.0.2", {"start": v(2.18, 51.5) * mm, "end": v(0, 56) * mm});
            skLineSegment(sketch, "E188.3.0.2", {"start": v(-1.95, 42.6) * mm, "end": v(0.23, 38.1) * mm});
            skLineSegment(sketch, "E188.6.0.2", {"start": v(1.95, 51.4) * mm, "end": v(-0.22, 55.9) * mm});
            skLineSegment(sketch, "E188.9.0.2", {"start": v(-2.4, 42.4) * mm, "end": v(-0.23, 37.9) * mm});
            skLineSegment(sketch, "E188.12.0.2", {"start": v(0, 47) * mm, "end": v(0, 38) * mm});
            skLineSegment(sketch, "E188.15.0.2", {"start": v(-2.18, 42.5) * mm, "end": v(0, 47) * mm});
            skLineSegment(sketch, "E188.18.0.2", {"start": v(-0.23, 47.1) * mm, "end": v(-2.4, 42.6) * mm});
            skLineSegment(sketch, "E188.21.0.2", {"start": v(0.22, 46.9) * mm, "end": v(-1.95, 42.4) * mm});
            skLineSegment(sketch, "E188.24.0.2", {"start": v(0.22, 56.1) * mm, "end": v(2.4, 51.6) * mm});
            skLineSegment(sketch, "E188.27.0.2", {"start": v(0.22, 46.9) * mm, "end": v(2.4, 51.4) * mm});
            skLineSegment(sketch, "E188.30.0.2", {"start": v(-0.23, 47.1) * mm, "end": v(1.95, 51.6) * mm});
            skLineSegment(sketch, "E188.33.0.2", {"start": v(0, 38) * mm, "end": v(-2.18, 42.5) * mm});
            skLineSegment(sketch, "E188.36.0.2", {"start": v(0, 38) * mm, "end": v(-2.18, 42.5) * mm});
            skLineSegment(sketch, "E188.39.0.2", {"start": v(0, 47) * mm, "end": v(0, 38) * mm});
            skLineSegment(sketch, "E188.42.0.2", {"start": v(-2.18, 42.5) * mm, "end": v(0, 47) * mm});
            skLineSegment(sketch, "E188.45.0.2", {"start": v(-2.18, 42.5) * mm, "end": v(0, 47) * mm});
            skLineSegment(sketch, "E188.48.0.2", {"start": v(0, 47) * mm, "end": v(0, 38) * mm});
            skLineSegment(sketch, "E188.51.0.2", {"start": v(0, 38) * mm, "end": v(-2.18, 42.5) * mm});
            skCircle(sketch, "E188.54.0.2", {"center": v(0, 56) * mm, "radius": 0.38 * mm});
            skCircle(sketch, "E188.56.0.2", {"center": v(2.18, 51.5) * mm, "radius": 0.38 * mm});
            skCircle(sketch, "E188.58.0.2", {"center": v(-2.18, 42.5) * mm, "radius": 0.38 * mm});
            skLineSegment(sketch, "E188.60.0.2", {"start": v(0, 56) * mm, "end": v(-0.23, 55.9) * mm});
            skLineSegment(sketch, "E188.63.0.2", {"start": v(0, 56) * mm, "end": v(0.22, 56.1) * mm});
            skLineSegment(sketch, "E188.66.0.2", {"start": v(2.18, 51.5) * mm, "end": v(2.4, 51.6) * mm});
            skLineSegment(sketch, "E188.69.0.2", {"start": v(1.95, 51.6) * mm, "end": v(2.4, 51.4) * mm});
            skLineSegment(sketch, "E188.72.0.2", {"start": v(2.18, 51.5) * mm, "end": v(1.95, 51.4) * mm});
            skLineSegment(sketch, "E188.75.0.2", {"start": v(0, 47) * mm, "end": v(0.22, 46.9) * mm});
            skLineSegment(sketch, "E188.78.0.2", {"start": v(-0.22, 47.1) * mm, "end": v(0.22, 46.9) * mm});
            skCircle(sketch, "E188.81.0.2", {"center": v(0, 47) * mm, "radius": 0.38 * mm});
            skLineSegment(sketch, "E188.83.0.2", {"start": v(0, 47) * mm, "end": v(-0.22, 47.1) * mm});
            skLineSegment(sketch, "E188.89.0.2", {"start": v(-2.18, 42.5) * mm, "end": v(-1.95, 42.6) * mm});
            skLineSegment(sketch, "E188.97.0.2", {"start": v(-2.18, 42.5) * mm, "end": v(-1.95, 42.4) * mm});
            skLineSegment(sketch, "E188.100.0.2", {"start": v(-2.18, 42.5) * mm, "end": v(-2.4, 42.4) * mm});
            skLineSegment(sketch, "E188.103.0.2", {"start": v(-2.18, 42.5) * mm, "end": v(-2.4, 42.6) * mm});
            skLineSegment(sketch, "E188.0.1.2", {"start": v(2.18, 51.5) * mm, "end": v(0, 56) * mm});
            skLineSegment(sketch, "E188.3.1.2", {"start": v(-1.95, 42.6) * mm, "end": v(0.23, 38.1) * mm});
            skLineSegment(sketch, "E188.6.1.2", {"start": v(1.95, 51.4) * mm, "end": v(-0.22, 55.9) * mm});
            skLineSegment(sketch, "E188.9.1.2", {"start": v(-2.4, 42.4) * mm, "end": v(-0.23, 37.9) * mm});
            skLineSegment(sketch, "E188.12.1.2", {"start": v(0, 47) * mm, "end": v(0, 38) * mm});
            skLineSegment(sketch, "E188.15.1.2", {"start": v(-2.18, 42.5) * mm, "end": v(0, 47) * mm});
            skLineSegment(sketch, "E188.18.1.2", {"start": v(-0.23, 47.1) * mm, "end": v(-2.4, 42.6) * mm});
            skLineSegment(sketch, "E188.21.1.2", {"start": v(0.22, 46.9) * mm, "end": v(-1.95, 42.4) * mm});
            skLineSegment(sketch, "E188.24.1.2", {"start": v(0.22, 56.1) * mm, "end": v(2.4, 51.6) * mm});
            skLineSegment(sketch, "E188.27.1.2", {"start": v(0.22, 46.9) * mm, "end": v(2.4, 51.4) * mm});
            skLineSegment(sketch, "E188.30.1.2", {"start": v(-0.23, 47.1) * mm, "end": v(1.95, 51.6) * mm});
            skLineSegment(sketch, "E188.33.1.2", {"start": v(0, 38) * mm, "end": v(-2.18, 42.5) * mm});
            skLineSegment(sketch, "E188.36.1.2", {"start": v(0, 38) * mm, "end": v(-2.18, 42.5) * mm});
            skLineSegment(sketch, "E188.39.1.2", {"start": v(0, 47) * mm, "end": v(0, 38) * mm});
            skLineSegment(sketch, "E188.42.1.2", {"start": v(-2.18, 42.5) * mm, "end": v(0, 47) * mm});
            skLineSegment(sketch, "E188.45.1.2", {"start": v(-2.18, 42.5) * mm, "end": v(0, 47) * mm});
            skLineSegment(sketch, "E188.48.1.2", {"start": v(0, 47) * mm, "end": v(0, 38) * mm});
            skLineSegment(sketch, "E188.51.1.2", {"start": v(0, 38) * mm, "end": v(-2.18, 42.5) * mm});
            skCircle(sketch, "E188.54.1.2", {"center": v(0, 56) * mm, "radius": 0.38 * mm});
            skCircle(sketch, "E188.56.1.2", {"center": v(2.18, 51.5) * mm, "radius": 0.38 * mm});
            skCircle(sketch, "E188.58.1.2", {"center": v(-2.18, 42.5) * mm, "radius": 0.38 * mm});
            skLineSegment(sketch, "E188.60.1.2", {"start": v(0, 56) * mm, "end": v(-0.23, 55.9) * mm});
            skLineSegment(sketch, "E188.63.1.2", {"start": v(0, 56) * mm, "end": v(0.22, 56.1) * mm});
            skLineSegment(sketch, "E188.66.1.2", {"start": v(2.18, 51.5) * mm, "end": v(2.4, 51.6) * mm});
            skLineSegment(sketch, "E188.69.1.2", {"start": v(1.95, 51.6) * mm, "end": v(2.4, 51.4) * mm});
            skLineSegment(sketch, "E188.72.1.2", {"start": v(2.18, 51.5) * mm, "end": v(1.95, 51.4) * mm});
            skLineSegment(sketch, "E188.75.1.2", {"start": v(0, 47) * mm, "end": v(0.22, 46.9) * mm});
            skLineSegment(sketch, "E188.78.1.2", {"start": v(-0.22, 47.1) * mm, "end": v(0.22, 46.9) * mm});
            skCircle(sketch, "E188.81.1.2", {"center": v(0, 47) * mm, "radius": 0.38 * mm});
            skLineSegment(sketch, "E188.83.1.2", {"start": v(0, 47) * mm, "end": v(-0.22, 47.1) * mm});
            skLineSegment(sketch, "E188.89.1.2", {"start": v(-2.18, 42.5) * mm, "end": v(-1.95, 42.6) * mm});
            skLineSegment(sketch, "E188.97.1.2", {"start": v(-2.18, 42.5) * mm, "end": v(-1.95, 42.4) * mm});
            skLineSegment(sketch, "E188.100.1.2", {"start": v(-2.18, 42.5) * mm, "end": v(-2.4, 42.4) * mm});
            skLineSegment(sketch, "E188.103.1.2", {"start": v(-2.18, 42.5) * mm, "end": v(-2.4, 42.6) * mm});
            skLineSegment(sketch, "E188.0.2.2", {"start": v(2.18, 51.5) * mm, "end": v(0, 56) * mm});
            skLineSegment(sketch, "E188.3.2.2", {"start": v(-1.95, 42.6) * mm, "end": v(0.23, 38.1) * mm});
            skLineSegment(sketch, "E188.6.2.2", {"start": v(1.95, 51.4) * mm, "end": v(-0.22, 55.9) * mm});
            skLineSegment(sketch, "E188.9.2.2", {"start": v(-2.4, 42.4) * mm, "end": v(-0.23, 37.9) * mm});
            skLineSegment(sketch, "E188.12.2.2", {"start": v(0, 47) * mm, "end": v(0, 38) * mm});
            skLineSegment(sketch, "E188.15.2.2", {"start": v(-2.18, 42.5) * mm, "end": v(0, 47) * mm});
            skLineSegment(sketch, "E188.18.2.2", {"start": v(-0.23, 47.1) * mm, "end": v(-2.4, 42.6) * mm});
            skLineSegment(sketch, "E188.21.2.2", {"start": v(0.22, 46.9) * mm, "end": v(-1.95, 42.4) * mm});
            skLineSegment(sketch, "E188.24.2.2", {"start": v(0.22, 56.1) * mm, "end": v(2.4, 51.6) * mm});
            skLineSegment(sketch, "E188.27.2.2", {"start": v(0.22, 46.9) * mm, "end": v(2.4, 51.4) * mm});
            skLineSegment(sketch, "E188.30.2.2", {"start": v(-0.23, 47.1) * mm, "end": v(1.95, 51.6) * mm});
            skLineSegment(sketch, "E188.33.2.2", {"start": v(0, 38) * mm, "end": v(-2.18, 42.5) * mm});
            skLineSegment(sketch, "E188.36.2.2", {"start": v(0, 38) * mm, "end": v(-2.18, 42.5) * mm});
            skLineSegment(sketch, "E188.39.2.2", {"start": v(0, 47) * mm, "end": v(0, 38) * mm});
            skLineSegment(sketch, "E188.42.2.2", {"start": v(-2.18, 42.5) * mm, "end": v(0, 47) * mm});
            skLineSegment(sketch, "E188.45.2.2", {"start": v(-2.18, 42.5) * mm, "end": v(0, 47) * mm});
            skLineSegment(sketch, "E188.48.2.2", {"start": v(0, 47) * mm, "end": v(0, 38) * mm});
            skLineSegment(sketch, "E188.51.2.2", {"start": v(0, 38) * mm, "end": v(-2.18, 42.5) * mm});
            skCircle(sketch, "E188.54.2.2", {"center": v(0, 56) * mm, "radius": 0.38 * mm});
            skCircle(sketch, "E188.56.2.2", {"center": v(2.18, 51.5) * mm, "radius": 0.38 * mm});
            skCircle(sketch, "E188.58.2.2", {"center": v(-2.18, 42.5) * mm, "radius": 0.38 * mm});
            skLineSegment(sketch, "E188.60.2.2", {"start": v(0, 56) * mm, "end": v(-0.23, 55.9) * mm});
            skLineSegment(sketch, "E188.63.2.2", {"start": v(0, 56) * mm, "end": v(0.22, 56.1) * mm});
            skLineSegment(sketch, "E188.66.2.2", {"start": v(2.18, 51.5) * mm, "end": v(2.4, 51.6) * mm});
            skLineSegment(sketch, "E188.69.2.2", {"start": v(1.95, 51.6) * mm, "end": v(2.4, 51.4) * mm});
            skLineSegment(sketch, "E188.72.2.2", {"start": v(2.18, 51.5) * mm, "end": v(1.95, 51.4) * mm});
            skLineSegment(sketch, "E188.75.2.2", {"start": v(0, 47) * mm, "end": v(0.22, 46.9) * mm});
            skLineSegment(sketch, "E188.78.2.2", {"start": v(-0.22, 47.1) * mm, "end": v(0.22, 46.9) * mm});
            skCircle(sketch, "E188.81.2.2", {"center": v(0, 47) * mm, "radius": 0.38 * mm});
            skLineSegment(sketch, "E188.83.2.2", {"start": v(0, 47) * mm, "end": v(-0.22, 47.1) * mm});
            skLineSegment(sketch, "E188.89.2.2", {"start": v(-2.18, 42.5) * mm, "end": v(-1.95, 42.6) * mm});
            skLineSegment(sketch, "E188.97.2.2", {"start": v(-2.18, 42.5) * mm, "end": v(-1.95, 42.4) * mm});
            skLineSegment(sketch, "E188.100.2.2", {"start": v(-2.18, 42.5) * mm, "end": v(-2.4, 42.4) * mm});
            skLineSegment(sketch, "E188.103.2.2", {"start": v(-2.18, 42.5) * mm, "end": v(-2.4, 42.6) * mm});
            skSolve(sketch);
        }
        {
            var Q0;
            {var subQ3=sQuery(id+"F8.wireOp",EDGE,"E154");var subQ7=sQuery(id+"F8.wireOp",EDGE,"E185");var subQ8=makeQuery(id+"F8.imprint","INTERSECT",VERTEX,{"derivedFrom":[subQ3,subQ7]});Q0=makeQuery(id+"F8.imprint","IMPRINT",FACE,{"disambiguationData":[TD([[makeQuery(id+"F8.imprint","IMPRINT",EDGE,{"disambiguationData":[TD([[subQ8,-1.0]])],"derivedFrom":subQ3}),-1.0]])]});}
            var Q1;
            {var subQ0=sQuery(id+"F8.wireOp",EDGE,"E171");var subQ1=sQuery(id+"F8.wireOp",EDGE,"E173");var subQ2=makeQuery(id+"F8.imprint","INTERSECT",VERTEX,{"derivedFrom":[subQ1,subQ0]});Q1=makeQuery(id+"F8.imprint","IMPRINT",FACE,{"disambiguationData":[TD([[makeQuery(id+"F8.imprint","IMPRINT",EDGE,{"disambiguationData":[TD([[subQ2,-1.0]])],"derivedFrom":subQ1}),1.0]])]});}
            var Q2;
            {var subQ0=sQuery(id+"F8.wireOp",EDGE,"E186.2.1.28");var subQ1=sQuery(id+"F8.wireOp",EDGE,"E186.2.1.9");var subQ2=makeQuery(id+"F8.imprint","INTERSECT",VERTEX,{"derivedFrom":[subQ1,subQ0]});Q2=makeQuery(id+"F8.imprint","IMPRINT",FACE,{"disambiguationData":[TD([[makeQuery(id+"F8.imprint","IMPRINT",EDGE,{"disambiguationData":[TD([[subQ2,-1.0]])],"derivedFrom":subQ1}),1.0]])]});}
            var Q3;
            {var subQ0=sQuery(id+"F8.wireOp",EDGE,"E186.2.1.28");var subQ1=sQuery(id+"F8.wireOp",EDGE,"E186.2.1.6");var subQ2=makeQuery(id+"F8.imprint","INTERSECT",VERTEX,{"derivedFrom":[subQ1,subQ0]});Q3=makeQuery(id+"F8.imprint","IMPRINT",FACE,{"disambiguationData":[TD([[makeQuery(id+"F8.imprint","IMPRINT",EDGE,{"disambiguationData":[TD([[subQ2,-1.0]])],"derivedFrom":subQ1}),1.0]])]});}
            var Q4;
            {var subQ0=sQuery(id+"F8.wireOp",EDGE,"E176");var subQ1=sQuery(id+"F8.wireOp",EDGE,"E177");var subQ2=makeQuery(id+"F8.imprint","INTERSECT",VERTEX,{"derivedFrom":[subQ1,subQ0]});Q4=makeQuery(id+"F8.imprint","IMPRINT",FACE,{"disambiguationData":[TD([[makeQuery(id+"F8.imprint","IMPRINT",EDGE,{"disambiguationData":[TD([[subQ2,-1.0]])],"derivedFrom":subQ1}),1.0]])]});}
            var Q5;
            {var subQ0=sQuery(id+"F8.wireOp",EDGE,"E176");var subQ1=sQuery(id+"F8.wireOp",EDGE,"E177");var subQ2=makeQuery(id+"F8.imprint","INTERSECT",VERTEX,{"derivedFrom":[subQ1,subQ0]});Q5=makeQuery(id+"F8.imprint","IMPRINT",FACE,{"disambiguationData":[TD([[makeQuery(id+"F8.imprint","IMPRINT",EDGE,{"disambiguationData":[TD([[subQ2,-1.0]])],"derivedFrom":subQ1}),-1.0]])]});}
            var Q6;
            {var subQ0=sQuery(id+"F8.wireOp",EDGE,"E186.2.1.20");var subQ1=sQuery(id+"F8.wireOp",EDGE,"E186.2.1.3");var subQ2=makeQuery(id+"F8.imprint","INTERSECT",VERTEX,{"derivedFrom":[subQ1,subQ0]});Q6=makeQuery(id+"F8.imprint","IMPRINT",FACE,{"disambiguationData":[TD([[makeQuery(id+"F8.imprint","IMPRINT",EDGE,{"disambiguationData":[TD([[subQ2,-1.0]])],"derivedFrom":subQ1}),1.0]])]});}
            var Q7;
            {var subQ0=sQuery(id+"F8.wireOp",EDGE,"E166");var subQ1=sQuery(id+"F8.wireOp",EDGE,"E161");var subQ2=makeQuery(id+"F8.imprint","INTERSECT",VERTEX,{"derivedFrom":[subQ1,subQ0]});Q7=makeQuery(id+"F8.imprint","IMPRINT",FACE,{"disambiguationData":[TD([[makeQuery(id+"F8.imprint","IMPRINT",EDGE,{"disambiguationData":[TD([[subQ2,-1.0]])],"derivedFrom":subQ1}),1.0]])]});}
            var Q8;
            {var subQ0=sQuery(id+"F8.wireOp",EDGE,"E166");var subQ1=sQuery(id+"F8.wireOp",EDGE,"E155");var subQ2=makeQuery(id+"F8.imprint","INTERSECT",VERTEX,{"derivedFrom":[subQ1,subQ0]});Q8=makeQuery(id+"F8.imprint","IMPRINT",FACE,{"disambiguationData":[TD([[makeQuery(id+"F8.imprint","IMPRINT",EDGE,{"disambiguationData":[TD([[subQ2,-1.0]])],"derivedFrom":subQ1}),1.0]])]});}
            var Q9;
            {var subQ3=sQuery(id+"F8.wireOp",EDGE,"E166");var subQ5=sQuery(id+"F8.wireOp",EDGE,"E155");var subQ6=makeQuery(id+"F8.imprint","INTERSECT",VERTEX,{"derivedFrom":[subQ5,subQ3]});Q9=makeQuery(id+"F8.imprint","IMPRINT",FACE,{"disambiguationData":[TD([[makeQuery(id+"F8.imprint","IMPRINT",EDGE,{"disambiguationData":[TD([[subQ6,-1.0]])],"derivedFrom":subQ5}),-1.0]])]});}
            var Q10;
            {var subQ5=sQuery(id+"F8.wireOp",EDGE,"E186.2.1.16");var subQ6=sQuery(id+"F8.wireOp",EDGE,"E186.2.1.1");var subQ7=makeQuery(id+"F8.imprint","INTERSECT",VERTEX,{"derivedFrom":[subQ6,subQ5]});Q10=makeQuery(id+"F8.imprint","IMPRINT",FACE,{"disambiguationData":[TD([[makeQuery(id+"F8.imprint","IMPRINT",EDGE,{"disambiguationData":[TD([[subQ7,1.0]])],"derivedFrom":subQ6}),-1.0]])]});}
            var Q11;
            {var subQ0=sQuery(id+"F8.wireOp",EDGE,"E186.2.1.16");var subQ1=sQuery(id+"F8.wireOp",EDGE,"E186.2.1.7");var subQ2=makeQuery(id+"F8.imprint","INTERSECT",VERTEX,{"derivedFrom":[subQ1,subQ0]});Q11=makeQuery(id+"F8.imprint","IMPRINT",FACE,{"disambiguationData":[TD([[makeQuery(id+"F8.imprint","IMPRINT",EDGE,{"disambiguationData":[TD([[subQ2,-1.0]])],"derivedFrom":subQ1}),-1.0]])]});}
            var Q12;
            {var subQ0=sQuery(id+"F8.wireOp",EDGE,"E186.2.1.19");var subQ1=sQuery(id+"F8.wireOp",EDGE,"E186.2.1.0");var subQ2=makeQuery(id+"F8.imprint","INTERSECT",VERTEX,{"derivedFrom":[subQ1,subQ0]});Q12=makeQuery(id+"F8.imprint","IMPRINT",FACE,{"disambiguationData":[TD([[makeQuery(id+"F8.imprint","IMPRINT",EDGE,{"disambiguationData":[TD([[subQ2,-1.0]])],"derivedFrom":subQ1}),1.0]])]});}
            var Q13;
            {var subQ0=sQuery(id+"F8.wireOp",EDGE,"E186.2.1.19");var subQ1=sQuery(id+"F8.wireOp",EDGE,"E186.2.1.0");var subQ2=makeQuery(id+"F8.imprint","INTERSECT",VERTEX,{"derivedFrom":[subQ1,subQ0]});Q13=makeQuery(id+"F8.imprint","IMPRINT",FACE,{"disambiguationData":[TD([[makeQuery(id+"F8.imprint","IMPRINT",EDGE,{"disambiguationData":[TD([[subQ2,-1.0]])],"derivedFrom":subQ1}),-1.0]])]});}
            var Q14;
            {var subQ5=sQuery(id+"F8.wireOp",EDGE,"E180");Q14=makeQuery(id+"F8.imprint","IMPRINT",FACE,{"disambiguationData":[TD([[makeQuery(id+"F8.imprint","IMPRINT",EDGE,{"derivedFrom":subQ5}),-1.0]])]});}
            var Q15;
            {var subQ0=sQuery(id+"F8.wireOp",EDGE,"E186.2.1.22");Q15=makeQuery(id+"F8.imprint","IMPRINT",FACE,{"disambiguationData":[TD([[makeQuery(id+"F8.imprint","IMPRINT",EDGE,{"derivedFrom":subQ0}),-1.0]])]});}
            var Q16;
            {var subQ0=sQuery(id+"F8.wireOp",EDGE,"E186.2.1.21");Q16=makeQuery(id+"F8.imprint","IMPRINT",FACE,{"disambiguationData":[TD([[makeQuery(id+"F8.imprint","IMPRINT",EDGE,{"derivedFrom":subQ0}),1.0]])]});}
            var Q17;
            {var subQ5=sQuery(id+"F8.wireOp",EDGE,"E186.2.1.21");Q17=makeQuery(id+"F8.imprint","IMPRINT",FACE,{"disambiguationData":[TD([[makeQuery(id+"F8.imprint","IMPRINT",EDGE,{"derivedFrom":subQ5}),-1.0]])]});}
            var Q18;
            {var subQ9=sQuery(id+"F8.wireOp",EDGE,"E179");Q18=makeQuery(id+"F8.imprint","IMPRINT",FACE,{"disambiguationData":[TD([[makeQuery(id+"F8.imprint","IMPRINT",EDGE,{"derivedFrom":subQ9}),1.0]])]});}
            var Q19;
            {var subQ0=sQuery(id+"F8.wireOp",EDGE,"E180");Q19=makeQuery(id+"F8.imprint","IMPRINT",FACE,{"disambiguationData":[TD([[makeQuery(id+"F8.imprint","IMPRINT",EDGE,{"derivedFrom":subQ0}),1.0]])]});}
            var Q20;
            {var subQ0=sQuery(id+"F8.wireOp",EDGE,"E179");Q20=makeQuery(id+"F8.imprint","IMPRINT",FACE,{"disambiguationData":[TD([[makeQuery(id+"F8.imprint","IMPRINT",EDGE,{"derivedFrom":subQ0}),-1.0]])]});}
            var Q21;
            {var subQ0=sQuery(id+"F8.wireOp",EDGE,"E176");var subQ1=sQuery(id+"F8.wireOp",EDGE,"E181");var subQ2=makeQuery(id+"F8.imprint","INTERSECT",VERTEX,{"derivedFrom":[subQ1,subQ0]});Q21=makeQuery(id+"F8.imprint","IMPRINT",FACE,{"disambiguationData":[TD([[makeQuery(id+"F8.imprint","IMPRINT",EDGE,{"disambiguationData":[TD([[subQ2,1.0]])],"derivedFrom":subQ1}),1.0]])]});}
            var Q22;
            {var subQ0=sQuery(id+"F8.wireOp",EDGE,"E176");var subQ1=sQuery(id+"F8.wireOp",EDGE,"E181");var subQ2=makeQuery(id+"F8.imprint","INTERSECT",VERTEX,{"derivedFrom":[subQ1,subQ0]});Q22=makeQuery(id+"F8.imprint","IMPRINT",FACE,{"disambiguationData":[TD([[makeQuery(id+"F8.imprint","IMPRINT",EDGE,{"disambiguationData":[TD([[subQ2,1.0]])],"derivedFrom":subQ1}),-1.0]])]});}
            var Q23;
            {var subQ1=sQuery(id+"F8.wireOp",EDGE,"E170");var subQ3=sQuery(id+"F8.wireOp",EDGE,"E171");var subQ4=makeQuery(id+"F8.imprint","INTERSECT",VERTEX,{"derivedFrom":[subQ1,subQ3]});Q23=makeQuery(id+"F8.imprint","IMPRINT",FACE,{"disambiguationData":[TD([[makeQuery(id+"F8.imprint","IMPRINT",EDGE,{"disambiguationData":[TD([[subQ4,-1.0]])],"derivedFrom":subQ3}),1.0]])]});}
            var Q24;
            {var subQ1=sQuery(id+"F8.wireOp",EDGE,"E168");var subQ3=sQuery(id+"F8.wireOp",EDGE,"E171");var subQ4=makeQuery(id+"F8.imprint","INTERSECT",VERTEX,{"derivedFrom":[subQ1,subQ3]});Q24=makeQuery(id+"F8.imprint","IMPRINT",FACE,{"disambiguationData":[TD([[makeQuery(id+"F8.imprint","IMPRINT",EDGE,{"disambiguationData":[TD([[subQ4,1.0]])],"derivedFrom":subQ3}),1.0]])]});}
            var Q25;
            {var subQ0=sQuery(id+"F8.wireOp",EDGE,"E167");Q25=makeQuery(id+"F8.imprint","IMPRINT",FACE,{"disambiguationData":[TD([[makeQuery(id+"F8.imprint","IMPRINT",EDGE,{"derivedFrom":subQ0}),1.0]])]});}
            var Q26;
            {var subQ9=sQuery(id+"F8.wireOp",EDGE,"E186.2.1.25");Q26=makeQuery(id+"F8.imprint","IMPRINT",FACE,{"disambiguationData":[TD([[makeQuery(id+"F8.imprint","IMPRINT",EDGE,{"derivedFrom":subQ9}),1.0]])]});}
            var Q27;
            {var subQ0=sQuery(id+"F8.wireOp",EDGE,"E171");var subQ1=sQuery(id+"F8.wireOp",EDGE,"E170");var subQ2=makeQuery(id+"F8.imprint","INTERSECT",VERTEX,{"derivedFrom":[subQ1,subQ0]});Q27=makeQuery(id+"F8.imprint","IMPRINT",FACE,{"disambiguationData":[TD([[makeQuery(id+"F8.imprint","IMPRINT",EDGE,{"disambiguationData":[TD([[subQ2,-1.0]])],"derivedFrom":subQ1}),-1.0]])]});}
            var Q28;
            {var subQ0=sQuery(id+"F8.wireOp",EDGE,"E172");Q28=makeQuery(id+"F8.imprint","IMPRINT",FACE,{"disambiguationData":[TD([[makeQuery(id+"F8.imprint","IMPRINT",EDGE,{"derivedFrom":subQ0}),1.0]])]});}
            var Q29;
            {var subQ0=sQuery(id+"F8.wireOp",EDGE,"E186.2.1.23");Q29=makeQuery(id+"F8.imprint","IMPRINT",FACE,{"disambiguationData":[TD([[makeQuery(id+"F8.imprint","IMPRINT",EDGE,{"derivedFrom":subQ0}),-1.0]])]});}
            var Q30;
            {var subQ0=sQuery(id+"F8.wireOp",EDGE,"E172");Q30=makeQuery(id+"F8.imprint","IMPRINT",FACE,{"disambiguationData":[TD([[makeQuery(id+"F8.imprint","IMPRINT",EDGE,{"derivedFrom":subQ0}),-1.0]])]});}
            var Q31;
            {var subQ0=sQuery(id+"F8.wireOp",EDGE,"E186.2.1.19");var subQ1=sQuery(id+"F8.wireOp",EDGE,"E186.2.1.2");var subQ2=makeQuery(id+"F8.imprint","INTERSECT",VERTEX,{"derivedFrom":[subQ1,subQ0]});Q31=makeQuery(id+"F8.imprint","IMPRINT",FACE,{"disambiguationData":[TD([[makeQuery(id+"F8.imprint","IMPRINT",EDGE,{"disambiguationData":[TD([[subQ2,1.0]])],"derivedFrom":subQ1}),-1.0]])]});}
            var Q32;
            {var subQ0=sQuery(id+"F8.wireOp",EDGE,"E186.2.1.25");Q32=makeQuery(id+"F8.imprint","IMPRINT",FACE,{"disambiguationData":[TD([[makeQuery(id+"F8.imprint","IMPRINT",EDGE,{"derivedFrom":subQ0}),-1.0]])]});}
            var Q33;
            {var subQ1=sQuery(id+"F8.wireOp",EDGE,"E155");var subQ3=sQuery(id+"F8.wireOp",EDGE,"E171");var subQ4=makeQuery(id+"F8.imprint","INTERSECT",VERTEX,{"derivedFrom":[subQ1,subQ3]});Q33=makeQuery(id+"F8.imprint","IMPRINT",FACE,{"disambiguationData":[TD([[makeQuery(id+"F8.imprint","IMPRINT",EDGE,{"disambiguationData":[TD([[subQ4,-1.0]])],"derivedFrom":subQ3}),1.0]])]});}
            var Q34;
            {var subQ0=sQuery(id+"F8.wireOp",EDGE,"E186.2.1.23");Q34=makeQuery(id+"F8.imprint","IMPRINT",FACE,{"disambiguationData":[TD([[makeQuery(id+"F8.imprint","IMPRINT",EDGE,{"derivedFrom":subQ0}),1.0]])]});}
            var Q35;
            {var subQ0=sQuery(id+"F8.wireOp",EDGE,"E186.2.1.19");var subQ1=sQuery(id+"F8.wireOp",EDGE,"E186.2.1.2");var subQ2=makeQuery(id+"F8.imprint","INTERSECT",VERTEX,{"derivedFrom":[subQ1,subQ0]});Q35=makeQuery(id+"F8.imprint","IMPRINT",FACE,{"disambiguationData":[TD([[makeQuery(id+"F8.imprint","IMPRINT",EDGE,{"disambiguationData":[TD([[subQ2,1.0]])],"derivedFrom":subQ1}),1.0]])]});}
            var Q36;
            {var subQ1=sQuery(id+"F8.wireOp",EDGE,"E163");var subQ3=sQuery(id+"F8.wireOp",EDGE,"E185");var subQ4=makeQuery(id+"F8.imprint","INTERSECT",VERTEX,{"derivedFrom":[subQ1,subQ3]});Q36=makeQuery(id+"F8.imprint","IMPRINT",FACE,{"disambiguationData":[TD([[makeQuery(id+"F8.imprint","IMPRINT",EDGE,{"disambiguationData":[TD([[subQ4,-1.0]])],"derivedFrom":subQ3}),-1.0]])]});}
            var Q37;
            {var subQ5=sQuery(id+"F8.wireOp",EDGE,"E160");Q37=makeQuery(id+"F8.imprint","IMPRINT",FACE,{"disambiguationData":[TD([[makeQuery(id+"F8.imprint","IMPRINT",EDGE,{"derivedFrom":subQ5}),-1.0]])]});}
            var Q38;
            {var subQ0=sQuery(id+"F8.wireOp",EDGE,"E160");Q38=makeQuery(id+"F8.imprint","IMPRINT",FACE,{"disambiguationData":[TD([[makeQuery(id+"F8.imprint","IMPRINT",EDGE,{"derivedFrom":subQ0}),1.0]])]});}
            var Q39;
            {var subQ0=sQuery(id+"F8.wireOp",EDGE,"E165");Q39=makeQuery(id+"F8.imprint","IMPRINT",FACE,{"disambiguationData":[TD([[makeQuery(id+"F8.imprint","IMPRINT",EDGE,{"derivedFrom":subQ0}),-1.0]])]});}
            var Q40;
            {var subQ5=sQuery(id+"F8.wireOp",EDGE,"E164");Q40=makeQuery(id+"F8.imprint","IMPRINT",FACE,{"disambiguationData":[TD([[makeQuery(id+"F8.imprint","IMPRINT",EDGE,{"derivedFrom":subQ5}),-1.0]])]});}
            var Q41;
            {var subQ7=sQuery(id+"F8.wireOp",EDGE,"E162");Q41=makeQuery(id+"F8.imprint","IMPRINT",FACE,{"disambiguationData":[TD([[makeQuery(id+"F8.imprint","IMPRINT",EDGE,{"derivedFrom":subQ7}),1.0]])]});}
            var Q42;
            {var subQ0=sQuery(id+"F8.wireOp",EDGE,"E170");var subQ1=sQuery(id+"F8.wireOp",EDGE,"E163");var subQ2=makeQuery(id+"F8.imprint","INTERSECT",VERTEX,{"derivedFrom":[subQ1,subQ0]});Q42=makeQuery(id+"F8.imprint","IMPRINT",FACE,{"disambiguationData":[TD([[makeQuery(id+"F8.imprint","IMPRINT",EDGE,{"disambiguationData":[TD([[subQ2,-1.0]])],"derivedFrom":subQ1}),1.0]])]});}
            var Q43;
            {var subQ0=sQuery(id+"F8.wireOp",EDGE,"E162");Q43=makeQuery(id+"F8.imprint","IMPRINT",FACE,{"disambiguationData":[TD([[makeQuery(id+"F8.imprint","IMPRINT",EDGE,{"derivedFrom":subQ0}),-1.0]])]});}
            var Q44;
            {var subQ0=sQuery(id+"F8.wireOp",EDGE,"E186.2.1.29");Q44=makeQuery(id+"F8.imprint","IMPRINT",FACE,{"disambiguationData":[TD([[makeQuery(id+"F8.imprint","IMPRINT",EDGE,{"derivedFrom":subQ0}),1.0]])]});}
            var Q45;
            {var subQ1=sQuery(id+"F8.wireOp",EDGE,"E186.2.1.15");var subQ3=sQuery(id+"F8.wireOp",EDGE,"E186.2.1.28");var subQ4=makeQuery(id+"F8.imprint","INTERSECT",VERTEX,{"derivedFrom":[subQ1,subQ3]});Q45=makeQuery(id+"F8.imprint","IMPRINT",FACE,{"disambiguationData":[TD([[makeQuery(id+"F8.imprint","IMPRINT",EDGE,{"disambiguationData":[TD([[subQ4,-1.0]])],"derivedFrom":subQ3}),1.0]])]});}
            var Q46;
            {var subQ1=sQuery(id+"F8.wireOp",EDGE,"E186.2.1.6");var subQ3=sQuery(id+"F8.wireOp",EDGE,"E186.2.1.28");var subQ4=makeQuery(id+"F8.imprint","INTERSECT",VERTEX,{"derivedFrom":[subQ1,subQ3]});Q46=makeQuery(id+"F8.imprint","IMPRINT",FACE,{"disambiguationData":[TD([[makeQuery(id+"F8.imprint","IMPRINT",EDGE,{"disambiguationData":[TD([[subQ4,1.0]])],"derivedFrom":subQ3}),1.0]])]});}
            var Q47;
            {var subQ1=sQuery(id+"F8.wireOp",EDGE,"E186.2.1.7");var subQ3=sQuery(id+"F8.wireOp",EDGE,"E186.2.1.28");var subQ4=makeQuery(id+"F8.imprint","INTERSECT",VERTEX,{"derivedFrom":[subQ1,subQ3]});Q47=makeQuery(id+"F8.imprint","IMPRINT",FACE,{"disambiguationData":[TD([[makeQuery(id+"F8.imprint","IMPRINT",EDGE,{"disambiguationData":[TD([[subQ4,-1.0]])],"derivedFrom":subQ3}),1.0]])]});}
            var Q48;
            {var subQ0=sQuery(id+"F8.wireOp",EDGE,"E186.2.1.27");Q48=makeQuery(id+"F8.imprint","IMPRINT",FACE,{"disambiguationData":[TD([[makeQuery(id+"F8.imprint","IMPRINT",EDGE,{"derivedFrom":subQ0}),-1.0]])]});}
            var Q49;
            {var subQ0=sQuery(id+"F8.wireOp",EDGE,"E186.2.1.28");var subQ1=sQuery(id+"F8.wireOp",EDGE,"E186.2.1.7");var subQ2=makeQuery(id+"F8.imprint","INTERSECT",VERTEX,{"derivedFrom":[subQ1,subQ0]});Q49=makeQuery(id+"F8.imprint","IMPRINT",FACE,{"disambiguationData":[TD([[makeQuery(id+"F8.imprint","IMPRINT",EDGE,{"disambiguationData":[TD([[subQ2,-1.0]])],"derivedFrom":subQ1}),-1.0]])]});}
            var Q50;
            {var subQ5=sQuery(id+"F8.wireOp",EDGE,"E186.2.1.27");Q50=makeQuery(id+"F8.imprint","IMPRINT",FACE,{"disambiguationData":[TD([[makeQuery(id+"F8.imprint","IMPRINT",EDGE,{"derivedFrom":subQ5}),1.0]])]});}
            var Q51;
            {var subQ5=sQuery(id+"F8.wireOp",EDGE,"E186.2.1.34");Q51=makeQuery(id+"F8.imprint","IMPRINT",FACE,{"disambiguationData":[TD([[makeQuery(id+"F8.imprint","IMPRINT",EDGE,{"derivedFrom":subQ5}),-1.0]])]});}
            var Q52;
            {var subQ0=sQuery(id+"F8.wireOp",EDGE,"E186.2.1.35");Q52=makeQuery(id+"F8.imprint","IMPRINT",FACE,{"disambiguationData":[TD([[makeQuery(id+"F8.imprint","IMPRINT",EDGE,{"derivedFrom":subQ0}),1.0]])]});}
            var Q53;
            {var subQ0=sQuery(id+"F8.wireOp",EDGE,"E186.2.1.35");Q53=makeQuery(id+"F8.imprint","IMPRINT",FACE,{"disambiguationData":[TD([[makeQuery(id+"F8.imprint","IMPRINT",EDGE,{"derivedFrom":subQ0}),-1.0]])]});}
            var Q54;
            {var subQ0=sQuery(id+"F8.wireOp",EDGE,"E186.2.1.7");var subQ1=sQuery(id+"F8.wireOp",EDGE,"E186.2.1.1");var subQ2=makeQuery(id+"F8.imprint","INTERSECT",VERTEX,{"derivedFrom":[subQ1,subQ0]});Q54=makeQuery(id+"F8.imprint","IMPRINT",FACE,{"disambiguationData":[TD([[makeQuery(id+"F8.imprint","IMPRINT",EDGE,{"disambiguationData":[TD([[subQ2,-1.0]])],"derivedFrom":subQ1}),1.0]])]});}
            var Q55;
            {var subQ0=sQuery(id+"F8.wireOp",EDGE,"E186.2.1.16");var subQ1=sQuery(id+"F8.wireOp",EDGE,"E186.2.1.1");var subQ2=makeQuery(id+"F8.imprint","INTERSECT",VERTEX,{"derivedFrom":[subQ1,subQ0]});Q55=makeQuery(id+"F8.imprint","IMPRINT",FACE,{"disambiguationData":[TD([[makeQuery(id+"F8.imprint","IMPRINT",EDGE,{"disambiguationData":[TD([[subQ2,-1.0]])],"derivedFrom":subQ1}),-1.0]])]});}
            var Q56;
            {var subQ5=sQuery(id+"F8.wireOp",EDGE,"E186.2.1.31");Q56=makeQuery(id+"F8.imprint","IMPRINT",FACE,{"disambiguationData":[TD([[makeQuery(id+"F8.imprint","IMPRINT",EDGE,{"derivedFrom":subQ5}),1.0]])]});}
            var Q57;
            {var subQ0=sQuery(id+"F8.wireOp",EDGE,"E186.2.1.36");Q57=makeQuery(id+"F8.imprint","IMPRINT",FACE,{"disambiguationData":[TD([[makeQuery(id+"F8.imprint","IMPRINT",EDGE,{"derivedFrom":subQ0}),-1.0]])]});}
            var Q58;
            {var subQ0=sQuery(id+"F8.wireOp",EDGE,"E186.2.1.31");Q58=makeQuery(id+"F8.imprint","IMPRINT",FACE,{"disambiguationData":[TD([[makeQuery(id+"F8.imprint","IMPRINT",EDGE,{"derivedFrom":subQ0}),-1.0]])]});}
            var Q59;
            {var subQ1=sQuery(id+"F8.wireOp",EDGE,"E183");var subQ3=sQuery(id+"F8.wireOp",EDGE,"E184");var subQ4=makeQuery(id+"F8.imprint","INTERSECT",VERTEX,{"derivedFrom":[subQ1,subQ3]});Q59=makeQuery(id+"F8.imprint","IMPRINT",FACE,{"disambiguationData":[TD([[makeQuery(id+"F8.imprint","IMPRINT",EDGE,{"disambiguationData":[TD([[subQ4,-1.0]])],"derivedFrom":subQ3}),1.0]])]});}
            var Q60;
            {var subQ1=sQuery(id+"F8.wireOp",EDGE,"E181");var subQ3=sQuery(id+"F8.wireOp",EDGE,"E184");var subQ4=makeQuery(id+"F8.imprint","INTERSECT",VERTEX,{"derivedFrom":[subQ1,subQ3]});Q60=makeQuery(id+"F8.imprint","IMPRINT",FACE,{"disambiguationData":[TD([[makeQuery(id+"F8.imprint","IMPRINT",EDGE,{"disambiguationData":[TD([[subQ4,1.0]])],"derivedFrom":subQ3}),1.0]])]});}
            var Q61;
            {var subQ0=sQuery(id+"F8.wireOp",EDGE,"E186.2.1.33");Q61=makeQuery(id+"F8.imprint","IMPRINT",FACE,{"disambiguationData":[TD([[makeQuery(id+"F8.imprint","IMPRINT",EDGE,{"derivedFrom":subQ0}),-1.0]])]});}
            var Q62;
            {var subQ0=sQuery(id+"F8.wireOp",EDGE,"E186.2.1.33");Q62=makeQuery(id+"F8.imprint","IMPRINT",FACE,{"disambiguationData":[TD([[makeQuery(id+"F8.imprint","IMPRINT",EDGE,{"derivedFrom":subQ0}),1.0]])]});}
            var Q63;
            {var subQ0=sQuery(id+"F8.wireOp",EDGE,"E182");Q63=makeQuery(id+"F8.imprint","IMPRINT",FACE,{"disambiguationData":[TD([[makeQuery(id+"F8.imprint","IMPRINT",EDGE,{"derivedFrom":subQ0}),-1.0]])]});}
            var Q64;
            {var subQ0=sQuery(id+"F8.wireOp",EDGE,"E182");Q64=makeQuery(id+"F8.imprint","IMPRINT",FACE,{"disambiguationData":[TD([[makeQuery(id+"F8.imprint","IMPRINT",EDGE,{"derivedFrom":subQ0}),1.0]])]});}
            var Q65;
            {var subQ1=sQuery(id+"F8.wireOp",EDGE,"E186.2.1.16");var subQ3=sQuery(id+"F8.wireOp",EDGE,"E184");var subQ4=makeQuery(id+"F8.imprint","INTERSECT",VERTEX,{"derivedFrom":[subQ1,subQ3]});Q65=makeQuery(id+"F8.imprint","IMPRINT",FACE,{"disambiguationData":[TD([[makeQuery(id+"F8.imprint","IMPRINT",EDGE,{"disambiguationData":[TD([[subQ4,-1.0]])],"derivedFrom":subQ3}),1.0]])]});}
            var Q66;
            {var subQ0=sQuery(id+"F8.wireOp",EDGE,"E158");Q66=makeQuery(id+"F8.imprint","IMPRINT",FACE,{"disambiguationData":[TD([[makeQuery(id+"F8.imprint","IMPRINT",EDGE,{"derivedFrom":subQ0}),1.0]])]});}
            var Q67;
            {var subQ0=sQuery(id+"F8.wireOp",EDGE,"E159");Q67=makeQuery(id+"F8.imprint","IMPRINT",FACE,{"disambiguationData":[TD([[makeQuery(id+"F8.imprint","IMPRINT",EDGE,{"derivedFrom":subQ0}),-1.0]])]});}
            var Q68;
            {var subQ0=sQuery(id+"F8.wireOp",EDGE,"E159");Q68=makeQuery(id+"F8.imprint","IMPRINT",FACE,{"disambiguationData":[TD([[makeQuery(id+"F8.imprint","IMPRINT",EDGE,{"derivedFrom":subQ0}),1.0]])]});}
            var Q69;
            {var subQ0=sQuery(id+"F8.wireOp",EDGE,"E158");Q69=makeQuery(id+"F8.imprint","IMPRINT",FACE,{"disambiguationData":[TD([[makeQuery(id+"F8.imprint","IMPRINT",EDGE,{"derivedFrom":subQ0}),-1.0]])]});}
            var Q70;
            {var subQ1=sQuery(id+"F8.wireOp",EDGE,"E154");var subQ3=sQuery(id+"F8.wireOp",EDGE,"E185");var subQ4=makeQuery(id+"F8.imprint","INTERSECT",VERTEX,{"derivedFrom":[subQ1,subQ3]});Q70=makeQuery(id+"F8.imprint","IMPRINT",FACE,{"disambiguationData":[TD([[makeQuery(id+"F8.imprint","IMPRINT",EDGE,{"disambiguationData":[TD([[subQ4,1.0]])],"derivedFrom":subQ3}),1.0]])]});}
            var Q71;
            {var subQ0=sQuery(id+"F8.wireOp",EDGE,"E188.81.2.2");var subQ1=sQuery(id+"F8.wireOp",EDGE,"E188.27.2.2");var subQ2=makeQuery(id+"F8.imprint","INTERSECT",VERTEX,{"derivedFrom":[subQ1,subQ0]});Q71=makeQuery(id+"F8.imprint","IMPRINT",FACE,{"disambiguationData":[TD([[makeQuery(id+"F8.imprint","IMPRINT",EDGE,{"disambiguationData":[TD([[subQ2,-1.0]])],"derivedFrom":subQ1}),1.0]])]});}
            var Q72;
            {var subQ5=sQuery(id+"F8.wireOp",EDGE,"E188.60.2.2");Q72=makeQuery(id+"F8.imprint","IMPRINT",FACE,{"disambiguationData":[TD([[makeQuery(id+"F8.imprint","IMPRINT",EDGE,{"derivedFrom":subQ5}),-1.0]])]});}
            var Q73;
            {var subQ0=sQuery(id+"F8.wireOp",EDGE,"E188.56.2.2");var subQ1=sQuery(id+"F8.wireOp",EDGE,"E188.0.2.2");var subQ2=makeQuery(id+"F8.imprint","INTERSECT",VERTEX,{"derivedFrom":[subQ1,subQ0]});Q73=makeQuery(id+"F8.imprint","IMPRINT",FACE,{"disambiguationData":[TD([[makeQuery(id+"F8.imprint","IMPRINT",EDGE,{"disambiguationData":[TD([[subQ2,-1.0]])],"derivedFrom":subQ1}),-1.0]])]});}
            var Q74;
            {var subQ0=sQuery(id+"F8.wireOp",EDGE,"E188.56.2.2");var subQ1=sQuery(id+"F8.wireOp",EDGE,"E188.0.2.2");var subQ2=makeQuery(id+"F8.imprint","INTERSECT",VERTEX,{"derivedFrom":[subQ1,subQ0]});Q74=makeQuery(id+"F8.imprint","IMPRINT",FACE,{"disambiguationData":[TD([[makeQuery(id+"F8.imprint","IMPRINT",EDGE,{"disambiguationData":[TD([[subQ2,-1.0]])],"derivedFrom":subQ1}),1.0]])]});}
            var Q75;
            {var subQ0=sQuery(id+"F8.wireOp",EDGE,"E188.60.2.2");Q75=makeQuery(id+"F8.imprint","IMPRINT",FACE,{"disambiguationData":[TD([[makeQuery(id+"F8.imprint","IMPRINT",EDGE,{"derivedFrom":subQ0}),1.0]])]});}
            var Q76;
            {var subQ0=sQuery(id+"F8.wireOp",EDGE,"E188.63.2.2");Q76=makeQuery(id+"F8.imprint","IMPRINT",FACE,{"disambiguationData":[TD([[makeQuery(id+"F8.imprint","IMPRINT",EDGE,{"derivedFrom":subQ0}),-1.0]])]});}
            var Q77;
            {var subQ5=sQuery(id+"F8.wireOp",EDGE,"E188.72.2.2");Q77=makeQuery(id+"F8.imprint","IMPRINT",FACE,{"disambiguationData":[TD([[makeQuery(id+"F8.imprint","IMPRINT",EDGE,{"derivedFrom":subQ5}),1.0]])]});}
            var Q78;
            {var subQ0=sQuery(id+"F8.wireOp",EDGE,"E188.66.2.2");Q78=makeQuery(id+"F8.imprint","IMPRINT",FACE,{"disambiguationData":[TD([[makeQuery(id+"F8.imprint","IMPRINT",EDGE,{"derivedFrom":subQ0}),-1.0]])]});}
            var Q79;
            {var subQ0=sQuery(id+"F8.wireOp",EDGE,"E188.66.2.2");Q79=makeQuery(id+"F8.imprint","IMPRINT",FACE,{"disambiguationData":[TD([[makeQuery(id+"F8.imprint","IMPRINT",EDGE,{"derivedFrom":subQ0}),1.0]])]});}
            var Q80;
            {var subQ0=sQuery(id+"F8.wireOp",EDGE,"E188.56.2.2");var subQ1=sQuery(id+"F8.wireOp",EDGE,"E188.6.2.2");var subQ2=makeQuery(id+"F8.imprint","INTERSECT",VERTEX,{"derivedFrom":[subQ1,subQ0]});Q80=makeQuery(id+"F8.imprint","IMPRINT",FACE,{"disambiguationData":[TD([[makeQuery(id+"F8.imprint","IMPRINT",EDGE,{"disambiguationData":[TD([[subQ2,1.0]])],"derivedFrom":subQ1}),-1.0]])]});}
            var Q81;
            {var subQ0=sQuery(id+"F8.wireOp",EDGE,"E188.56.2.2");var subQ1=sQuery(id+"F8.wireOp",EDGE,"E188.6.2.2");var subQ2=makeQuery(id+"F8.imprint","INTERSECT",VERTEX,{"derivedFrom":[subQ1,subQ0]});Q81=makeQuery(id+"F8.imprint","IMPRINT",FACE,{"disambiguationData":[TD([[makeQuery(id+"F8.imprint","IMPRINT",EDGE,{"disambiguationData":[TD([[subQ2,1.0]])],"derivedFrom":subQ1}),1.0]])]});}
            var Q82;
            {var subQ0=sQuery(id+"F8.wireOp",EDGE,"E188.72.2.2");Q82=makeQuery(id+"F8.imprint","IMPRINT",FACE,{"disambiguationData":[TD([[makeQuery(id+"F8.imprint","IMPRINT",EDGE,{"derivedFrom":subQ0}),-1.0]])]});}
            var Q83;
            {var subQ0=sQuery(id+"F8.wireOp",EDGE,"E188.78.2.2");Q83=makeQuery(id+"F8.imprint","IMPRINT",FACE,{"disambiguationData":[TD([[makeQuery(id+"F8.imprint","IMPRINT",EDGE,{"derivedFrom":subQ0}),1.0]])]});}
            var Q84;
            {var subQ1=sQuery(id+"F8.wireOp",EDGE,"E188.18.2.2");var subQ3=sQuery(id+"F8.wireOp",EDGE,"E188.81.2.2");var subQ4=makeQuery(id+"F8.imprint","INTERSECT",VERTEX,{"derivedFrom":[subQ1,subQ3]});Q84=makeQuery(id+"F8.imprint","IMPRINT",FACE,{"disambiguationData":[TD([[makeQuery(id+"F8.imprint","IMPRINT",EDGE,{"disambiguationData":[TD([[subQ4,1.0]])],"derivedFrom":subQ3}),1.0]])]});}
            var Q85;
            {var subQ0=sQuery(id+"F8.wireOp",EDGE,"E188.83.2.2");Q85=makeQuery(id+"F8.imprint","IMPRINT",FACE,{"disambiguationData":[TD([[makeQuery(id+"F8.imprint","IMPRINT",EDGE,{"derivedFrom":subQ0}),1.0]])]});}
            var Q86;
            {var subQ1=sQuery(id+"F8.wireOp",EDGE,"E188.45.2.2");var subQ3=sQuery(id+"F8.wireOp",EDGE,"E188.81.2.2");var subQ4=makeQuery(id+"F8.imprint","INTERSECT",VERTEX,{"derivedFrom":[subQ1,subQ3]});Q86=makeQuery(id+"F8.imprint","IMPRINT",FACE,{"disambiguationData":[TD([[makeQuery(id+"F8.imprint","IMPRINT",EDGE,{"disambiguationData":[TD([[subQ4,-1.0]])],"derivedFrom":subQ3}),1.0]])]});}
            var Q87;
            {var subQ0=sQuery(id+"F8.wireOp",EDGE,"E188.78.2.2");Q87=makeQuery(id+"F8.imprint","IMPRINT",FACE,{"disambiguationData":[TD([[makeQuery(id+"F8.imprint","IMPRINT",EDGE,{"derivedFrom":subQ0}),-1.0]])]});}
            var Q88;
            {var subQ1=sQuery(id+"F8.wireOp",EDGE,"E188.21.2.2");var subQ3=sQuery(id+"F8.wireOp",EDGE,"E188.81.2.2");var subQ4=makeQuery(id+"F8.imprint","INTERSECT",VERTEX,{"derivedFrom":[subQ1,subQ3]});Q88=makeQuery(id+"F8.imprint","IMPRINT",FACE,{"disambiguationData":[TD([[makeQuery(id+"F8.imprint","IMPRINT",EDGE,{"disambiguationData":[TD([[subQ4,-1.0]])],"derivedFrom":subQ3}),1.0]])]});}
            var Q89;
            {var subQ1=sQuery(id+"F8.wireOp",EDGE,"E188.21.2.2");var subQ7=sQuery(id+"F8.wireOp",EDGE,"E188.48.2.2");var subQ8=makeQuery(id+"F8.imprint","INTERSECT",VERTEX,{"derivedFrom":[subQ1,subQ7]});Q89=makeQuery(id+"F8.imprint","IMPRINT",FACE,{"disambiguationData":[TD([[makeQuery(id+"F8.imprint","IMPRINT",EDGE,{"disambiguationData":[TD([[subQ8,-1.0]])],"derivedFrom":subQ1}),-1.0]])]});}
            var Q90;
            {var subQ0=sQuery(id+"F8.wireOp",EDGE,"E188.81.2.2");var subQ1=sQuery(id+"F8.wireOp",EDGE,"E188.21.2.2");var subQ2=makeQuery(id+"F8.imprint","INTERSECT",VERTEX,{"derivedFrom":[subQ1,subQ0]});Q90=makeQuery(id+"F8.imprint","IMPRINT",FACE,{"disambiguationData":[TD([[makeQuery(id+"F8.imprint","IMPRINT",EDGE,{"disambiguationData":[TD([[subQ2,-1.0]])],"derivedFrom":subQ1}),-1.0]])]});}
            var Q91;
            {var subQ0=sQuery(id+"F8.wireOp",EDGE,"E188.81.2.2");var subQ1=sQuery(id+"F8.wireOp",EDGE,"E188.18.2.2");var subQ2=makeQuery(id+"F8.imprint","INTERSECT",VERTEX,{"derivedFrom":[subQ1,subQ0]});Q91=makeQuery(id+"F8.imprint","IMPRINT",FACE,{"disambiguationData":[TD([[makeQuery(id+"F8.imprint","IMPRINT",EDGE,{"disambiguationData":[TD([[subQ2,-1.0]])],"derivedFrom":subQ1}),1.0]])]});}
            var Q92;
            {var subQ0=sQuery(id+"F8.wireOp",EDGE,"E188.103.2.2");Q92=makeQuery(id+"F8.imprint","IMPRINT",FACE,{"disambiguationData":[TD([[makeQuery(id+"F8.imprint","IMPRINT",EDGE,{"derivedFrom":subQ0}),-1.0]])]});}
            var Q93;
            {var subQ0=sQuery(id+"F8.wireOp",EDGE,"E188.89.2.2");Q93=makeQuery(id+"F8.imprint","IMPRINT",FACE,{"disambiguationData":[TD([[makeQuery(id+"F8.imprint","IMPRINT",EDGE,{"derivedFrom":subQ0}),1.0]])]});}
            var Q94;
            {var subQ0=sQuery(id+"F8.wireOp",EDGE,"E188.21.2.2");var subQ1=sQuery(id+"F8.wireOp",EDGE,"E188.3.2.2");var subQ2=makeQuery(id+"F8.imprint","INTERSECT",VERTEX,{"derivedFrom":[subQ1,subQ0]});Q94=makeQuery(id+"F8.imprint","IMPRINT",FACE,{"disambiguationData":[TD([[makeQuery(id+"F8.imprint","IMPRINT",EDGE,{"disambiguationData":[TD([[subQ2,-1.0]])],"derivedFrom":subQ1}),1.0]])]});}
            var Q95;
            {var subQ5=sQuery(id+"F8.wireOp",EDGE,"E188.97.2.2");Q95=makeQuery(id+"F8.imprint","IMPRINT",FACE,{"disambiguationData":[TD([[makeQuery(id+"F8.imprint","IMPRINT",EDGE,{"derivedFrom":subQ5}),-1.0]])]});}
            var Q96;
            {var subQ0=sQuery(id+"F8.wireOp",EDGE,"E188.89.2.2");Q96=makeQuery(id+"F8.imprint","IMPRINT",FACE,{"disambiguationData":[TD([[makeQuery(id+"F8.imprint","IMPRINT",EDGE,{"derivedFrom":subQ0}),-1.0]])]});}
            var Q97;
            {var subQ0=sQuery(id+"F8.wireOp",EDGE,"E188.100.2.2");Q97=makeQuery(id+"F8.imprint","IMPRINT",FACE,{"disambiguationData":[TD([[makeQuery(id+"F8.imprint","IMPRINT",EDGE,{"derivedFrom":subQ0}),1.0]])]});}
            var Q98;
            {var subQ0=sQuery(id+"F8.wireOp",EDGE,"E188.100.2.2");Q98=makeQuery(id+"F8.imprint","IMPRINT",FACE,{"disambiguationData":[TD([[makeQuery(id+"F8.imprint","IMPRINT",EDGE,{"derivedFrom":subQ0}),-1.0]])]});}
            var Q99;
            {var subQ0=sQuery(id+"F8.wireOp",EDGE,"E188.58.2.2");var subQ1=sQuery(id+"F8.wireOp",EDGE,"E188.9.2.2");var subQ2=makeQuery(id+"F8.imprint","INTERSECT",VERTEX,{"derivedFrom":[subQ1,subQ0]});Q99=makeQuery(id+"F8.imprint","IMPRINT",FACE,{"disambiguationData":[TD([[makeQuery(id+"F8.imprint","IMPRINT",EDGE,{"disambiguationData":[TD([[subQ2,-1.0]])],"derivedFrom":subQ1}),1.0]])]});}
            var Q100;
            {var subQ5=sQuery(id+"F8.wireOp",EDGE,"E188.48.2.2");var subQ6=sQuery(id+"F8.wireOp",EDGE,"E188.3.2.2");var subQ7=makeQuery(id+"F8.imprint","INTERSECT",VERTEX,{"derivedFrom":[subQ6,subQ5]});Q100=makeQuery(id+"F8.imprint","IMPRINT",FACE,{"disambiguationData":[TD([[makeQuery(id+"F8.imprint","IMPRINT",EDGE,{"disambiguationData":[TD([[subQ7,1.0]])],"derivedFrom":subQ6}),-1.0]])]});}
            var Q101;
            {var subQ1=sQuery(id+"F8.wireOp",EDGE,"E186.2.1.2");var subQ3=sQuery(id+"F8.wireOp",EDGE,"E186.0.1.18");var subQ4=makeQuery(id+"F8.imprint","INTERSECT",VERTEX,{"derivedFrom":[subQ1,subQ3]});Q101=makeQuery(id+"F8.imprint","IMPRINT",FACE,{"disambiguationData":[TD([[makeQuery(id+"F8.imprint","IMPRINT",EDGE,{"disambiguationData":[TD([[subQ4,1.0]])],"derivedFrom":subQ3}),1.0]])]});}
            var Q102;
            {var subQ0=sQuery(id+"F8.wireOp",EDGE,"E186.0.1.21");Q102=makeQuery(id+"F8.imprint","IMPRINT",FACE,{"disambiguationData":[TD([[makeQuery(id+"F8.imprint","IMPRINT",EDGE,{"derivedFrom":subQ0}),1.0]])]});}
            var Q103;
            {var subQ0=sQuery(id+"F8.wireOp",EDGE,"E186.0.1.21");Q103=makeQuery(id+"F8.imprint","IMPRINT",FACE,{"disambiguationData":[TD([[makeQuery(id+"F8.imprint","IMPRINT",EDGE,{"derivedFrom":subQ0}),-1.0]])]});}
            var Q104;
            {var subQ1=sQuery(id+"F8.wireOp",EDGE,"E188.48.2.2");var subQ3=sQuery(id+"F8.wireOp",EDGE,"E186.0.1.18");var subQ4=makeQuery(id+"F8.imprint","INTERSECT",VERTEX,{"derivedFrom":[subQ1,subQ3]});Q104=makeQuery(id+"F8.imprint","IMPRINT",FACE,{"disambiguationData":[TD([[makeQuery(id+"F8.imprint","IMPRINT",EDGE,{"disambiguationData":[TD([[subQ4,-1.0]])],"derivedFrom":subQ3}),1.0]])]});}
            var Q105;
            {var subQ0=sQuery(id+"F8.wireOp",EDGE,"E186.0.1.22");Q105=makeQuery(id+"F8.imprint","IMPRINT",FACE,{"disambiguationData":[TD([[makeQuery(id+"F8.imprint","IMPRINT",EDGE,{"derivedFrom":subQ0}),1.0]])]});}
            var Q106;
            {var subQ1=sQuery(id+"F8.wireOp",EDGE,"E186.2.1.8");var subQ3=sQuery(id+"F8.wireOp",EDGE,"E186.0.1.18");var subQ4=makeQuery(id+"F8.imprint","INTERSECT",VERTEX,{"derivedFrom":[subQ1,subQ3]});Q106=makeQuery(id+"F8.imprint","IMPRINT",FACE,{"disambiguationData":[TD([[makeQuery(id+"F8.imprint","IMPRINT",EDGE,{"disambiguationData":[TD([[subQ4,-1.0]])],"derivedFrom":subQ3}),1.0]])]});}
            var Q107;
            {var subQ0=sQuery(id+"F8.wireOp",EDGE,"E186.0.1.22");Q107=makeQuery(id+"F8.imprint","IMPRINT",FACE,{"disambiguationData":[TD([[makeQuery(id+"F8.imprint","IMPRINT",EDGE,{"derivedFrom":subQ0}),-1.0]])]});}
            extrude(context, id + "F9", {"entities" : qUnion([Q0, Q1, Q2, Q3, Q4, Q5, Q6, Q7, Q8, Q9, Q10, Q11, Q12, Q13, Q14, Q15, Q16, Q17, Q18, Q19, Q20, Q21, Q22, Q23, Q24, Q25, Q26, Q27, Q28, Q29, Q30, Q31, Q32, Q33, Q34, Q35, Q36, Q37, Q38, Q39, Q40, Q41, Q42, Q43, Q44, Q45, Q46, Q47, Q48, Q49, Q50, Q51, Q52, Q53, Q54, Q55, Q56, Q57, Q58, Q59, Q60, Q61, Q62, Q63, Q64, Q65, Q66, Q67, Q68, Q69, Q70, Q71, Q72, Q73, Q74, Q75, Q76, Q77, Q78, Q79, Q80, Q81, Q82, Q83, Q84, Q85, Q86, Q87, Q88, Q89, Q90, Q91, Q92, Q93, Q94, Q95, Q96, Q97, Q98, Q99, Q100, Q101, Q102, Q103, Q104, Q105, Q106, Q107]), "operationType" : NewBodyOperationType.ADD, "depth" : 30 * mm});
        }
        {
            var Q0;
            Q0=qCreatedBy(makeId("Right.planeOp"),FACE);
            var sketch = newSketch(context, id + "F10", { "sketchPlane" : qUnion([Q0])});
            skLineSegment(sketch, "E189", {"start": v(0, 0) * mm, "end": v(0, 30) * mm});
            skLineSegment(sketch, "E190", {"start": v(0, 0) * mm, "end": v(0, 10) * mm});
            skLineSegment(sketch, "E191", {"start": v(0, 10) * mm, "end": v(0, 20) * mm});
            skLineSegment(sketch, "E192", {"start": v(0, 20) * mm, "end": v(0, 30) * mm});
            skLineSegment(sketch, "E193", {"start": v(0, 20) * mm, "end": v(2, 20) * mm});
            skLineSegment(sketch, "E194", {"start": v(2, 20) * mm, "end": v(2, 21) * mm});
            skLineSegment(sketch, "E195", {"start": v(2, 20) * mm, "end": v(2, 19) * mm});
            skLineSegment(sketch, "E196.bottom", {"start": v(2, 19) * mm, "end": v(2, 19) * mm});
            skLineSegment(sketch, "E196.top", {"start": v(2, 21) * mm, "end": v(2, 21) * mm});
            skLineSegment(sketch, "E196.left", {"start": v(2, 19) * mm, "end": v(2, 21) * mm});
            skLineSegment(sketch, "E196.right", {"start": v(2, 19) * mm, "end": v(2, 21) * mm});
            skLineSegment(sketch, "E197", {"start": v(2, 19) * mm, "end": v(43.97, 19) * mm});
            skLineSegment(sketch, "E198.bottom", {"start": v(43.97, 19) * mm, "end": v(2, 19) * mm});
            skLineSegment(sketch, "E198.top", {"start": v(43.97, 21) * mm, "end": v(2, 21) * mm});
            skLineSegment(sketch, "E198.left", {"start": v(43.97, 19) * mm, "end": v(43.97, 21) * mm});
            skLineSegment(sketch, "E199", {"start": v(0, 10) * mm, "end": v(2, 10) * mm});
            skLineSegment(sketch, "E200", {"start": v(2, 10) * mm, "end": v(2, 11) * mm});
            skLineSegment(sketch, "E201", {"start": v(2, 11) * mm, "end": v(44.86, 11) * mm});
            skLineSegment(sketch, "E202", {"start": v(44.86, 11) * mm, "end": v(44.86, 9) * mm});
            skLineSegment(sketch, "E203", {"start": v(44.86, 9) * mm, "end": v(2, 9) * mm});
            skLineSegment(sketch, "E204", {"start": v(2, 9) * mm, "end": v(2, 10) * mm});
            skLineSegment(sketch, "E205", {"start": v(44.86, 9) * mm, "end": v(62.62, 9) * mm});
            skLineSegment(sketch, "E206", {"start": v(44.86, 11) * mm, "end": v(60.88, 11.27) * mm});
            skLineSegment(sketch, "E207", {"start": v(60.88, 11.27) * mm, "end": v(62.62, 9) * mm});
            skLineSegment(sketch, "E208", {"start": v(43.97, 19) * mm, "end": v(60.47, 19) * mm});
            skLineSegment(sketch, "E209", {"start": v(60.47, 19) * mm, "end": v(60.47, 21) * mm});
            skLineSegment(sketch, "E210", {"start": v(60.47, 21) * mm, "end": v(43.97, 21) * mm});
            skSolve(sketch);
        }
        {
            var Q0;
            {var subQ2=sQuery(id+"F10.wireOp",EDGE,"E198.bottom");Q0=makeQuery(id+"F10.imprint","IMPRINT",FACE,{"disambiguationData":[TD([[makeQuery(id+"F10.imprint","IMPRINT",EDGE,{"derivedFrom":subQ2}),-1.0]])]});}
            var Q1;
            Q1=makeQuery(id+"F10.imprint","IMPRINT",FACE,{"disambiguationData":[TD([[makeQuery(id+"F10.imprint","IMPRINT",EDGE,{"derivedFrom":sQuery(id+"F10.wireOp",EDGE,"E200")}),-1.0]])]});
            var Q2;
            Q2=makeQuery(id+"F10.imprint","IMPRINT",FACE,{"disambiguationData":[TD([[makeQuery(id+"F10.imprint","IMPRINT",EDGE,{"derivedFrom":sQuery(id+"F10.wireOp",EDGE,"E202")}),1.0]])]});
            var Q3;
            Q3=makeQuery(id+"F10.imprint","IMPRINT",FACE,{"disambiguationData":[TD([[makeQuery(id+"F10.imprint","IMPRINT",EDGE,{"derivedFrom":sQuery(id+"F10.wireOp",EDGE,"E198.left")}),-1.0]])]});
            extrude(context, id + "F11", {"entities" : qUnion([Q0, Q1, Q2, Q3]), "operationType" : NewBodyOperationType.REMOVE, "oppositeDirection" : true, "depth" : 25 * mm, "hasSecondDirection" : true, "secondDirectionOppositeDirection" : false, "secondDirectionDepth" : 25 * mm});
        }
    });
